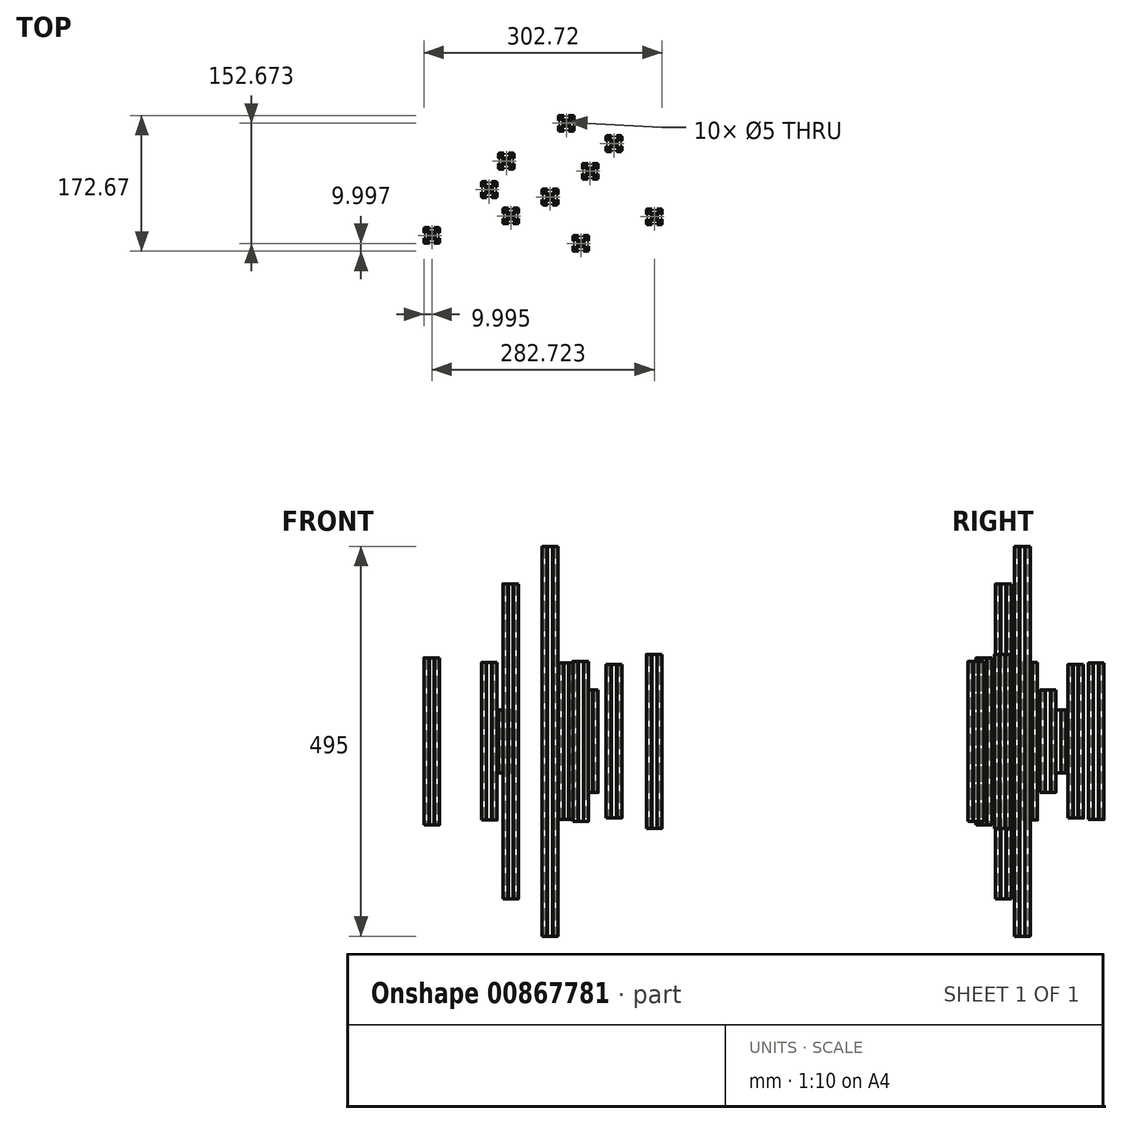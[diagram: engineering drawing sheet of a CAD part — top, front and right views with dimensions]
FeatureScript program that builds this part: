
annotation { "Feature Type Name" : "Feature", "Feature Type Description" : "" }
export const myFeature = defineFeature(function(context is Context, id is Id, definition is map)
    precondition{}
    {
        {
            var Q0;
            Q0=qCreatedBy(makeId("Top.planeOp"),FACE);
            var sketch = newSketch(context, id + "F0", { "sketchPlane" : qUnion([Q0])});
            skCircle(sketch, "E0", {"center": v(-10.22, 3.28) * mm, "radius": 2.5 * mm});
            skLineSegment(sketch, "E1.bottom", {"start": v(-1.72, -6.72) * mm, "end": v(-6.12, -6.72) * mm});
            skLineSegment(sketch, "E1.top", {"start": v(-1.72, 13.28) * mm, "end": v(-6.12, 13.28) * mm});
            skLineSegment(sketch, "E1.left", {"start": v(-0.22, -5.22) * mm, "end": v(-0.22, -0.32) * mm});
            skLineSegment(sketch, "E2.bottom", {"start": v(-8.21, -0.62) * mm, "end": v(-12.24, -0.62) * mm});
            skLineSegment(sketch, "E2.top", {"start": v(-8.21, 7.18) * mm, "end": v(-12.24, 7.18) * mm});
            skLineSegment(sketch, "E2.left", {"start": v(-6.32, 1.27) * mm, "end": v(-6.32, 5.3) * mm});
            skLineSegment(sketch, "E2.right", {"start": v(-14.12, 1.27) * mm, "end": v(-14.12, 5.3) * mm});
            skLineSegment(sketch, "E3.bottom", {"start": v(-1.72, 13.28) * mm, "end": v(-4.72, 13.28) * mm});
            skLineSegment(sketch, "E3.left", {"start": v(-0.22, 11.78) * mm, "end": v(-0.22, 8.78) * mm});
            skLineSegment(sketch, "E3.right", {"start": v(-4.72, 11.48) * mm, "end": v(-4.72, 9.84) * mm});
            skLineSegment(sketch, "E4", {"start": v(-5.74, 6.7) * mm, "end": v(-3.66, 8.78) * mm});
            skLineSegment(sketch, "E5.MirrorCS", {"start": v(-6.8, 7.77) * mm, "end": v(-4.72, 9.84) * mm});
            skLineSegment(sketch, "E6", {"start": v(-2.02, 8.78) * mm, "end": v(-2.02, 6.38) * mm});
            skLineSegment(sketch, "E7", {"start": v(-0.52, 6.88) * mm, "end": v(-0.22, 6.88) * mm});
            skLineSegment(sketch, "E8", {"start": v(-2.02, 6.38) * mm, "end": v(-0.72, 6.38) * mm});
            skLineSegment(sketch, "E9", {"start": v(-0.72, 6.68) * mm, "end": v(-0.72, 6.38) * mm});
            skPoint(sketch, "E10.visualSharp", {"position": v(-0.72, 6.88) * mm});
            skArc(sketch, "E10.filletArc", {"start": v(-0.52, 6.88) * mm, "mid": v(-0.67, 6.82) * mm, "end": v(-0.72, 6.68) * mm});
            skPoint(sketch, "E11.newPointA", {"position": v(-6.32, 6.12) * mm});
            skArc(sketch, "E11.filletArc", {"start": v(-5.74, 6.7) * mm, "mid": v(-6.17, 6.06) * mm, "end": v(-6.32, 5.3) * mm});
            skPoint(sketch, "E12.newPointA", {"position": v(-7.39, 7.18) * mm});
            skPoint(sketch, "E12.newPointB", {"position": v(-6.32, 7.18) * mm});
            skArc(sketch, "E12.filletArc", {"start": v(-8.21, 7.18) * mm, "mid": v(-7.45, 7.33) * mm, "end": v(-6.8, 7.77) * mm});
            skLineSegment(sketch, "E13.MirrorCS", {"start": v(-4.72, 11.48) * mm, "end": v(-7.12, 11.48) * mm});
            skLineSegment(sketch, "E14.MirrorCS", {"start": v(-7.12, 11.48) * mm, "end": v(-7.12, 12.78) * mm});
            skPoint(sketch, "E15.visualSharp", {"position": v(-0.22, 13.28) * mm});
            skArc(sketch, "E15.filletArc", {"start": v(-0.22, 11.78) * mm, "mid": v(-0.66, 12.84) * mm, "end": v(-1.72, 13.28) * mm});
            skLineSegment(sketch, "E16.trimOffspring", {"start": v(-2.02, 8.78) * mm, "end": v(-3.66, 8.78) * mm});
            skLineSegment(sketch, "E17.MirrorCS", {"start": v(-0.52, -0.32) * mm, "end": v(-0.22, -0.32) * mm});
            skArc(sketch, "E18.MirrorCS", {"start": v(-0.52, -0.32) * mm, "mid": v(-0.67, -0.26) * mm, "end": v(-0.72, -0.12) * mm});
            skLineSegment(sketch, "E19.MirrorCS", {"start": v(-0.72, -0.12) * mm, "end": v(-0.72, 0.18) * mm});
            skArc(sketch, "E20.MirrorCS", {"start": v(-5.74, -0.14) * mm, "mid": v(-6.17, 0.5) * mm, "end": v(-6.32, 1.27) * mm});
            skLineSegment(sketch, "E21.MirrorCS", {"start": v(-2.02, -2.22) * mm, "end": v(-3.66, -2.22) * mm});
            skLineSegment(sketch, "E22.MirrorCS", {"start": v(-2.02, 0.18) * mm, "end": v(-0.72, 0.18) * mm});
            skLineSegment(sketch, "E23.MirrorCS", {"start": v(-1.72, -6.72) * mm, "end": v(-4.72, -6.72) * mm});
            skPoint(sketch, "E24.MirrorP", {"position": v(-0.72, -0.32) * mm});
            skLineSegment(sketch, "E25.MirrorCS", {"start": v(-7.12, -4.92) * mm, "end": v(-7.12, -6.22) * mm});
            skLineSegment(sketch, "E26.MirrorCS", {"start": v(-4.72, -4.92) * mm, "end": v(-7.12, -4.92) * mm});
            skLineSegment(sketch, "E27.MirrorCS", {"start": v(-2.02, -2.22) * mm, "end": v(-2.02, 0.18) * mm});
            skLineSegment(sketch, "E28.MirrorCS", {"start": v(-0.22, -5.22) * mm, "end": v(-0.22, -2.22) * mm});
            skLineSegment(sketch, "E29.MirrorCS", {"start": v(-5.74, -0.14) * mm, "end": v(-3.66, -2.22) * mm});
            skPoint(sketch, "E30.MirrorP", {"position": v(-6.32, 0.44) * mm});
            skPoint(sketch, "E31.MirrorP", {"position": v(-0.22, -6.72) * mm});
            skPoint(sketch, "E32.MirrorP", {"position": v(-6.32, -0.62) * mm});
            skLineSegment(sketch, "E33.MirrorCS", {"start": v(-6.8, -1.2) * mm, "end": v(-4.72, -3.28) * mm});
            skPoint(sketch, "E34.MirrorP", {"position": v(-7.39, -0.62) * mm});
            skArc(sketch, "E35.MirrorCS", {"start": v(-0.22, -5.22) * mm, "mid": v(-0.66, -6.28) * mm, "end": v(-1.72, -6.72) * mm});
            skLineSegment(sketch, "E36.MirrorCS", {"start": v(-4.72, -4.92) * mm, "end": v(-4.72, -3.28) * mm});
            skArc(sketch, "E37.MirrorCS", {"start": v(-8.21, -0.62) * mm, "mid": v(-7.45, -0.77) * mm, "end": v(-6.8, -1.2) * mm});
            skLineSegment(sketch, "E38.trimOffspring", {"start": v(-0.22, 6.88) * mm, "end": v(-0.22, 11.78) * mm});
            skLineSegment(sketch, "E39.MirrorCS", {"start": v(-6.62, 12.98) * mm, "end": v(-6.62, 13.28) * mm});
            skArc(sketch, "E40.MirrorCS", {"start": v(-6.62, 12.98) * mm, "mid": v(-6.68, 12.84) * mm, "end": v(-6.82, 12.78) * mm});
            skLineSegment(sketch, "E41.MirrorCS", {"start": v(-6.82, 12.78) * mm, "end": v(-7.12, 12.78) * mm});
            skLineSegment(sketch, "E42", {"start": v(-6.12, 13.28) * mm, "end": v(-6.62, 13.28) * mm});
            skLineSegment(sketch, "E43.MirrorCS", {"start": v(-6.62, -6.42) * mm, "end": v(-6.62, -6.72) * mm});
            skLineSegment(sketch, "E44.MirrorCS", {"start": v(-6.82, -6.22) * mm, "end": v(-7.12, -6.22) * mm});
            skLineSegment(sketch, "E45.MirrorCS", {"start": v(-6.12, -6.72) * mm, "end": v(-6.62, -6.72) * mm});
            skArc(sketch, "E46.MirrorCS", {"start": v(-6.62, -6.42) * mm, "mid": v(-6.68, -6.28) * mm, "end": v(-6.82, -6.22) * mm});
            skArc(sketch, "E47.MirrorCS", {"start": v(-19.92, -0.32) * mm, "mid": v(-19.78, -0.26) * mm, "end": v(-19.72, -0.12) * mm});
            skLineSegment(sketch, "E48.MirrorCS", {"start": v(-19.92, 6.88) * mm, "end": v(-20.22, 6.88) * mm});
            skLineSegment(sketch, "E49.MirrorCS", {"start": v(-19.72, -0.12) * mm, "end": v(-19.72, 0.18) * mm});
            skArc(sketch, "E50.MirrorCS", {"start": v(-19.92, 6.88) * mm, "mid": v(-19.78, 6.82) * mm, "end": v(-19.72, 6.68) * mm});
            skLineSegment(sketch, "E51.MirrorCS", {"start": v(-19.72, 6.68) * mm, "end": v(-19.72, 6.38) * mm});
            skLineSegment(sketch, "E52.MirrorCS", {"start": v(-19.92, -0.32) * mm, "end": v(-20.22, -0.32) * mm});
            skLineSegment(sketch, "E53.MirrorCS", {"start": v(-14.32, 13.28) * mm, "end": v(-13.82, 13.28) * mm});
            skArc(sketch, "E54.MirrorCS", {"start": v(-20.22, -5.22) * mm, "mid": v(-19.79, -6.28) * mm, "end": v(-18.72, -6.72) * mm});
            skLineSegment(sketch, "E55.MirrorCS", {"start": v(-13.82, 12.98) * mm, "end": v(-13.82, 13.28) * mm});
            skArc(sketch, "E56.MirrorCS", {"start": v(-14.71, 6.7) * mm, "mid": v(-14.28, 6.06) * mm, "end": v(-14.12, 5.3) * mm});
            skLineSegment(sketch, "E57.MirrorCS", {"start": v(-13.62, -6.22) * mm, "end": v(-13.32, -6.22) * mm});
            skLineSegment(sketch, "E58.MirrorCS", {"start": v(-13.32, 11.48) * mm, "end": v(-13.32, 12.78) * mm});
            skLineSegment(sketch, "E59.MirrorCS", {"start": v(-12.24, 7.18) * mm, "end": v(-8.21, 7.18) * mm});
            skLineSegment(sketch, "E60.MirrorCS", {"start": v(-18.42, 0.18) * mm, "end": v(-19.72, 0.18) * mm});
            skLineSegment(sketch, "E61.MirrorCS", {"start": v(-18.42, 6.38) * mm, "end": v(-19.72, 6.38) * mm});
            skLineSegment(sketch, "E62.MirrorCS", {"start": v(-13.62, 12.78) * mm, "end": v(-13.32, 12.78) * mm});
            skArc(sketch, "E63.MirrorCS", {"start": v(-14.71, -0.14) * mm, "mid": v(-14.28, 0.5) * mm, "end": v(-14.12, 1.27) * mm});
            skArc(sketch, "E64.MirrorCS", {"start": v(-13.82, -6.42) * mm, "mid": v(-13.77, -6.28) * mm, "end": v(-13.62, -6.22) * mm});
            skArc(sketch, "E65.MirrorCS", {"start": v(-13.82, 12.98) * mm, "mid": v(-13.77, 12.84) * mm, "end": v(-13.62, 12.78) * mm});
            skLineSegment(sketch, "E66.MirrorCS", {"start": v(-13.82, -6.42) * mm, "end": v(-13.82, -6.72) * mm});
            skLineSegment(sketch, "E67.MirrorCS", {"start": v(-12.24, -0.62) * mm, "end": v(-8.21, -0.62) * mm});
            skLineSegment(sketch, "E68.MirrorCS", {"start": v(-14.32, -6.72) * mm, "end": v(-13.82, -6.72) * mm});
            skLineSegment(sketch, "E69.MirrorCS", {"start": v(-13.32, -4.92) * mm, "end": v(-13.32, -6.22) * mm});
            skArc(sketch, "E70.MirrorCS", {"start": v(-12.24, 7.18) * mm, "mid": v(-13, 7.33) * mm, "end": v(-13.65, 7.77) * mm});
            skPoint(sketch, "E71.MirrorP", {"position": v(-20.22, -6.72) * mm});
            skLineSegment(sketch, "E72.MirrorCS", {"start": v(-18.72, -6.72) * mm, "end": v(-14.32, -6.72) * mm});
            skPoint(sketch, "E73.MirrorP", {"position": v(-14.12, -0.62) * mm});
            skLineSegment(sketch, "E74.MirrorCS", {"start": v(-18.72, 13.28) * mm, "end": v(-14.32, 13.28) * mm});
            skArc(sketch, "E75.MirrorCS", {"start": v(-12.24, -0.62) * mm, "mid": v(-13, -0.77) * mm, "end": v(-13.65, -1.2) * mm});
            skArc(sketch, "E76.MirrorCS", {"start": v(-20.22, 11.78) * mm, "mid": v(-19.79, 12.84) * mm, "end": v(-18.72, 13.28) * mm});
            skPoint(sketch, "E77.MirrorP", {"position": v(-14.12, 0.44) * mm});
            skLineSegment(sketch, "E78.MirrorCS", {"start": v(-15.72, 11.48) * mm, "end": v(-15.72, 9.84) * mm});
            skLineSegment(sketch, "E79.MirrorCS", {"start": v(-13.65, 7.77) * mm, "end": v(-15.72, 9.84) * mm});
            skPoint(sketch, "E80.MirrorP", {"position": v(-14.12, 6.12) * mm});
            skLineSegment(sketch, "E81.MirrorCS", {"start": v(-18.42, -2.22) * mm, "end": v(-18.42, 0.18) * mm});
            skLineSegment(sketch, "E82.MirrorCS", {"start": v(-14.71, -0.14) * mm, "end": v(-16.79, -2.22) * mm});
            skLineSegment(sketch, "E83.MirrorCS", {"start": v(-15.72, -4.92) * mm, "end": v(-13.32, -4.92) * mm});
            skLineSegment(sketch, "E84.MirrorCS", {"start": v(-18.42, -2.22) * mm, "end": v(-16.79, -2.22) * mm});
            skLineSegment(sketch, "E85.MirrorCS", {"start": v(-20.22, -5.22) * mm, "end": v(-20.22, -2.22) * mm});
            skLineSegment(sketch, "E86.MirrorCS", {"start": v(-18.72, 13.28) * mm, "end": v(-15.72, 13.28) * mm});
            skLineSegment(sketch, "E87.MirrorCS", {"start": v(-20.22, 6.88) * mm, "end": v(-20.22, 11.78) * mm});
            skLineSegment(sketch, "E88.MirrorCS", {"start": v(-15.72, 11.48) * mm, "end": v(-13.32, 11.48) * mm});
            skLineSegment(sketch, "E89.MirrorCS", {"start": v(-13.65, -1.2) * mm, "end": v(-15.72, -3.28) * mm});
            skPoint(sketch, "E90.MirrorP", {"position": v(-13.06, -0.62) * mm});
            skLineSegment(sketch, "E91.MirrorCS", {"start": v(-18.42, 8.78) * mm, "end": v(-18.42, 6.38) * mm});
            skLineSegment(sketch, "E92.MirrorCS", {"start": v(-20.22, 11.78) * mm, "end": v(-20.22, 8.78) * mm});
            skPoint(sketch, "E93.MirrorP", {"position": v(-19.72, -0.32) * mm});
            skPoint(sketch, "E94.MirrorP", {"position": v(-20.22, 13.28) * mm});
            skPoint(sketch, "E95.MirrorP", {"position": v(-19.72, 6.88) * mm});
            skLineSegment(sketch, "E96.MirrorCS", {"start": v(-14.71, 6.7) * mm, "end": v(-16.79, 8.78) * mm});
            skLineSegment(sketch, "E97.MirrorCS", {"start": v(-18.42, 8.78) * mm, "end": v(-16.79, 8.78) * mm});
            skLineSegment(sketch, "E98.MirrorCS", {"start": v(-20.22, -5.22) * mm, "end": v(-20.22, -0.32) * mm});
            skLineSegment(sketch, "E99.MirrorCS", {"start": v(-18.72, -6.72) * mm, "end": v(-15.72, -6.72) * mm});
            skPoint(sketch, "E100.MirrorP", {"position": v(-14.12, 7.18) * mm});
            skPoint(sketch, "E101.MirrorP", {"position": v(-13.06, 7.18) * mm});
            skLineSegment(sketch, "E102.MirrorCS", {"start": v(-15.72, -4.92) * mm, "end": v(-15.72, -3.28) * mm});
            skSolve(sketch);
        }
        {
            var Q0;
            Q0=makeQuery(id+"F0.imprint","IMPRINT",FACE,{"disambiguationData":[TD([[makeQuery(id+"F0.imprint","IMPRINT",EDGE,{"derivedFrom":sQuery(id+"F0.wireOp",EDGE,"E1.bottom")}),-1.0]])]});
            extrude(context, id + "F1", {"entities" : qUnion([Q0]), "endBound" : BoundingType.SYMMETRIC, "depth" : 495 * mm, "offsetDistance" : 25 * mm});
        }
        {
            var Q0;
            Q0=qCreatedBy(makeId("Top.planeOp"),FACE);
            var sketch = newSketch(context, id + "F2", { "sketchPlane" : qUnion([Q0])});
            skCircle(sketch, "E103", {"center": v(-87.46, 12.57) * mm, "radius": 2.5 * mm});
            skLineSegment(sketch, "E104.bottom", {"start": v(-78.96, 2.57) * mm, "end": v(-83.36, 2.57) * mm});
            skLineSegment(sketch, "E104.top", {"start": v(-78.96, 22.57) * mm, "end": v(-83.36, 22.57) * mm});
            skLineSegment(sketch, "E104.left", {"start": v(-77.46, 4.07) * mm, "end": v(-77.46, 8.97) * mm});
            skLineSegment(sketch, "E105.bottom", {"start": v(-85.45, 8.67) * mm, "end": v(-89.47, 8.67) * mm});
            skLineSegment(sketch, "E105.top", {"start": v(-85.45, 16.47) * mm, "end": v(-89.47, 16.47) * mm});
            skLineSegment(sketch, "E105.left", {"start": v(-83.56, 10.56) * mm, "end": v(-83.56, 14.58) * mm});
            skLineSegment(sketch, "E105.right", {"start": v(-91.36, 10.56) * mm, "end": v(-91.36, 14.58) * mm});
            skLineSegment(sketch, "E106.bottom", {"start": v(-78.96, 22.57) * mm, "end": v(-81.96, 22.57) * mm});
            skLineSegment(sketch, "E106.left", {"start": v(-77.46, 21.07) * mm, "end": v(-77.46, 18.07) * mm});
            skLineSegment(sketch, "E106.right", {"start": v(-81.96, 20.77) * mm, "end": v(-81.96, 19.13) * mm});
            skLineSegment(sketch, "E107", {"start": v(-82.97, 16) * mm, "end": v(-80.9, 18.07) * mm});
            skLineSegment(sketch, "E108.MirrorCS", {"start": v(-84.04, 17.06) * mm, "end": v(-81.96, 19.13) * mm});
            skLineSegment(sketch, "E109", {"start": v(-79.26, 18.07) * mm, "end": v(-79.26, 15.67) * mm});
            skLineSegment(sketch, "E110", {"start": v(-77.76, 16.17) * mm, "end": v(-77.46, 16.17) * mm});
            skLineSegment(sketch, "E111", {"start": v(-79.26, 15.67) * mm, "end": v(-77.96, 15.67) * mm});
            skLineSegment(sketch, "E112", {"start": v(-77.96, 15.97) * mm, "end": v(-77.96, 15.67) * mm});
            skPoint(sketch, "E113.visualSharp", {"position": v(-77.96, 16.17) * mm});
            skArc(sketch, "E113.filletArc", {"start": v(-77.76, 16.17) * mm, "mid": v(-77.9, 16.11) * mm, "end": v(-77.96, 15.97) * mm});
            skPoint(sketch, "E114.newPointA", {"position": v(-83.56, 15.4) * mm});
            skArc(sketch, "E114.filletArc", {"start": v(-82.97, 16) * mm, "mid": v(-83.4, 15.35) * mm, "end": v(-83.56, 14.58) * mm});
            skPoint(sketch, "E115.newPointA", {"position": v(-84.62, 16.47) * mm});
            skPoint(sketch, "E115.newPointB", {"position": v(-83.56, 16.47) * mm});
            skArc(sketch, "E115.filletArc", {"start": v(-85.45, 16.47) * mm, "mid": v(-84.68, 16.62) * mm, "end": v(-84.04, 17.06) * mm});
            skLineSegment(sketch, "E116.MirrorCS", {"start": v(-81.96, 20.77) * mm, "end": v(-84.36, 20.77) * mm});
            skLineSegment(sketch, "E117.MirrorCS", {"start": v(-84.36, 20.77) * mm, "end": v(-84.36, 22.07) * mm});
            skPoint(sketch, "E118.visualSharp", {"position": v(-77.46, 22.57) * mm});
            skArc(sketch, "E118.filletArc", {"start": v(-77.46, 21.07) * mm, "mid": v(-77.9, 22.13) * mm, "end": v(-78.96, 22.57) * mm});
            skLineSegment(sketch, "E119.trimOffspring", {"start": v(-79.26, 18.07) * mm, "end": v(-80.9, 18.07) * mm});
            skLineSegment(sketch, "E120.MirrorCS", {"start": v(-77.76, 8.97) * mm, "end": v(-77.46, 8.97) * mm});
            skArc(sketch, "E121.MirrorCS", {"start": v(-77.76, 8.97) * mm, "mid": v(-77.9, 9.03) * mm, "end": v(-77.96, 9.17) * mm});
            skLineSegment(sketch, "E122.MirrorCS", {"start": v(-77.96, 9.17) * mm, "end": v(-77.96, 9.47) * mm});
            skArc(sketch, "E123.MirrorCS", {"start": v(-82.97, 9.15) * mm, "mid": v(-83.4, 9.8) * mm, "end": v(-83.56, 10.56) * mm});
            skLineSegment(sketch, "E124.MirrorCS", {"start": v(-79.26, 7.07) * mm, "end": v(-80.9, 7.07) * mm});
            skLineSegment(sketch, "E125.MirrorCS", {"start": v(-79.26, 9.47) * mm, "end": v(-77.96, 9.47) * mm});
            skLineSegment(sketch, "E126.MirrorCS", {"start": v(-78.96, 2.57) * mm, "end": v(-81.96, 2.57) * mm});
            skPoint(sketch, "E127.MirrorP", {"position": v(-77.96, 8.97) * mm});
            skLineSegment(sketch, "E128.MirrorCS", {"start": v(-84.36, 4.37) * mm, "end": v(-84.36, 3.07) * mm});
            skLineSegment(sketch, "E129.MirrorCS", {"start": v(-81.96, 4.37) * mm, "end": v(-84.36, 4.37) * mm});
            skLineSegment(sketch, "E130.MirrorCS", {"start": v(-79.26, 7.07) * mm, "end": v(-79.26, 9.47) * mm});
            skLineSegment(sketch, "E131.MirrorCS", {"start": v(-77.46, 4.07) * mm, "end": v(-77.46, 7.07) * mm});
            skLineSegment(sketch, "E132.MirrorCS", {"start": v(-82.97, 9.15) * mm, "end": v(-80.9, 7.07) * mm});
            skPoint(sketch, "E133.MirrorP", {"position": v(-83.56, 9.73) * mm});
            skPoint(sketch, "E134.MirrorP", {"position": v(-77.46, 2.57) * mm});
            skPoint(sketch, "E135.MirrorP", {"position": v(-83.56, 8.67) * mm});
            skLineSegment(sketch, "E136.MirrorCS", {"start": v(-84.04, 8.08) * mm, "end": v(-81.96, 6) * mm});
            skPoint(sketch, "E137.MirrorP", {"position": v(-84.62, 8.67) * mm});
            skArc(sketch, "E138.MirrorCS", {"start": v(-77.46, 4.07) * mm, "mid": v(-77.9, 3) * mm, "end": v(-78.96, 2.57) * mm});
            skLineSegment(sketch, "E139.MirrorCS", {"start": v(-81.96, 4.37) * mm, "end": v(-81.96, 6) * mm});
            skArc(sketch, "E140.MirrorCS", {"start": v(-85.45, 8.67) * mm, "mid": v(-84.68, 8.52) * mm, "end": v(-84.04, 8.08) * mm});
            skLineSegment(sketch, "E141.trimOffspring", {"start": v(-77.46, 16.17) * mm, "end": v(-77.46, 21.07) * mm});
            skLineSegment(sketch, "E142.MirrorCS", {"start": v(-83.86, 22.27) * mm, "end": v(-83.86, 22.57) * mm});
            skArc(sketch, "E143.MirrorCS", {"start": v(-83.86, 22.27) * mm, "mid": v(-83.92, 22.13) * mm, "end": v(-84.06, 22.07) * mm});
            skLineSegment(sketch, "E144.MirrorCS", {"start": v(-84.06, 22.07) * mm, "end": v(-84.36, 22.07) * mm});
            skLineSegment(sketch, "E145", {"start": v(-83.36, 22.57) * mm, "end": v(-83.86, 22.57) * mm});
            skLineSegment(sketch, "E146.MirrorCS", {"start": v(-83.86, 2.87) * mm, "end": v(-83.86, 2.57) * mm});
            skLineSegment(sketch, "E147.MirrorCS", {"start": v(-84.06, 3.07) * mm, "end": v(-84.36, 3.07) * mm});
            skLineSegment(sketch, "E148.MirrorCS", {"start": v(-83.36, 2.57) * mm, "end": v(-83.86, 2.57) * mm});
            skArc(sketch, "E149.MirrorCS", {"start": v(-83.86, 2.87) * mm, "mid": v(-83.92, 3.01) * mm, "end": v(-84.06, 3.07) * mm});
            skArc(sketch, "E150.MirrorCS", {"start": v(-97.16, 8.97) * mm, "mid": v(-97.02, 9.03) * mm, "end": v(-96.96, 9.17) * mm});
            skLineSegment(sketch, "E151.MirrorCS", {"start": v(-97.16, 16.17) * mm, "end": v(-97.46, 16.17) * mm});
            skLineSegment(sketch, "E152.MirrorCS", {"start": v(-96.96, 9.17) * mm, "end": v(-96.96, 9.47) * mm});
            skArc(sketch, "E153.MirrorCS", {"start": v(-97.16, 16.17) * mm, "mid": v(-97.02, 16.11) * mm, "end": v(-96.96, 15.97) * mm});
            skLineSegment(sketch, "E154.MirrorCS", {"start": v(-96.96, 15.97) * mm, "end": v(-96.96, 15.67) * mm});
            skLineSegment(sketch, "E155.MirrorCS", {"start": v(-97.16, 8.97) * mm, "end": v(-97.46, 8.97) * mm});
            skLineSegment(sketch, "E156.MirrorCS", {"start": v(-91.56, 22.57) * mm, "end": v(-91.06, 22.57) * mm});
            skArc(sketch, "E157.MirrorCS", {"start": v(-97.46, 4.07) * mm, "mid": v(-97.02, 3) * mm, "end": v(-95.96, 2.57) * mm});
            skLineSegment(sketch, "E158.MirrorCS", {"start": v(-91.06, 22.27) * mm, "end": v(-91.06, 22.57) * mm});
            skArc(sketch, "E159.MirrorCS", {"start": v(-91.95, 16) * mm, "mid": v(-91.51, 15.35) * mm, "end": v(-91.36, 14.58) * mm});
            skLineSegment(sketch, "E160.MirrorCS", {"start": v(-90.86, 3.07) * mm, "end": v(-90.56, 3.07) * mm});
            skLineSegment(sketch, "E161.MirrorCS", {"start": v(-90.56, 20.77) * mm, "end": v(-90.56, 22.07) * mm});
            skLineSegment(sketch, "E162.MirrorCS", {"start": v(-89.47, 16.47) * mm, "end": v(-85.45, 16.47) * mm});
            skLineSegment(sketch, "E163.MirrorCS", {"start": v(-95.66, 9.47) * mm, "end": v(-96.96, 9.47) * mm});
            skLineSegment(sketch, "E164.MirrorCS", {"start": v(-95.66, 15.67) * mm, "end": v(-96.96, 15.67) * mm});
            skLineSegment(sketch, "E165.MirrorCS", {"start": v(-90.86, 22.07) * mm, "end": v(-90.56, 22.07) * mm});
            skArc(sketch, "E166.MirrorCS", {"start": v(-91.95, 9.15) * mm, "mid": v(-91.51, 9.8) * mm, "end": v(-91.36, 10.56) * mm});
            skArc(sketch, "E167.MirrorCS", {"start": v(-91.06, 2.87) * mm, "mid": v(-91, 3.01) * mm, "end": v(-90.86, 3.07) * mm});
            skArc(sketch, "E168.MirrorCS", {"start": v(-91.06, 22.27) * mm, "mid": v(-91, 22.13) * mm, "end": v(-90.86, 22.07) * mm});
            skLineSegment(sketch, "E169.MirrorCS", {"start": v(-91.06, 2.87) * mm, "end": v(-91.06, 2.57) * mm});
            skLineSegment(sketch, "E170.MirrorCS", {"start": v(-89.47, 8.67) * mm, "end": v(-85.45, 8.67) * mm});
            skLineSegment(sketch, "E171.MirrorCS", {"start": v(-91.56, 2.57) * mm, "end": v(-91.06, 2.57) * mm});
            skLineSegment(sketch, "E172.MirrorCS", {"start": v(-90.56, 4.37) * mm, "end": v(-90.56, 3.07) * mm});
            skArc(sketch, "E173.MirrorCS", {"start": v(-89.47, 16.47) * mm, "mid": v(-90.24, 16.62) * mm, "end": v(-90.89, 17.06) * mm});
            skPoint(sketch, "E174.MirrorP", {"position": v(-97.46, 2.57) * mm});
            skLineSegment(sketch, "E175.MirrorCS", {"start": v(-95.96, 2.57) * mm, "end": v(-91.56, 2.57) * mm});
            skPoint(sketch, "E176.MirrorP", {"position": v(-91.36, 8.67) * mm});
            skLineSegment(sketch, "E177.MirrorCS", {"start": v(-95.96, 22.57) * mm, "end": v(-91.56, 22.57) * mm});
            skArc(sketch, "E178.MirrorCS", {"start": v(-89.47, 8.67) * mm, "mid": v(-90.24, 8.52) * mm, "end": v(-90.89, 8.08) * mm});
            skArc(sketch, "E179.MirrorCS", {"start": v(-97.46, 21.07) * mm, "mid": v(-97.02, 22.13) * mm, "end": v(-95.96, 22.57) * mm});
            skPoint(sketch, "E180.MirrorP", {"position": v(-91.36, 9.73) * mm});
            skLineSegment(sketch, "E181.MirrorCS", {"start": v(-92.96, 20.77) * mm, "end": v(-92.96, 19.13) * mm});
            skLineSegment(sketch, "E182.MirrorCS", {"start": v(-90.89, 17.06) * mm, "end": v(-92.96, 19.13) * mm});
            skPoint(sketch, "E183.MirrorP", {"position": v(-91.36, 15.4) * mm});
            skLineSegment(sketch, "E184.MirrorCS", {"start": v(-95.66, 7.07) * mm, "end": v(-95.66, 9.47) * mm});
            skLineSegment(sketch, "E185.MirrorCS", {"start": v(-91.95, 9.15) * mm, "end": v(-94.02, 7.07) * mm});
            skLineSegment(sketch, "E186.MirrorCS", {"start": v(-92.96, 4.37) * mm, "end": v(-90.56, 4.37) * mm});
            skLineSegment(sketch, "E187.MirrorCS", {"start": v(-95.66, 7.07) * mm, "end": v(-94.02, 7.07) * mm});
            skLineSegment(sketch, "E188.MirrorCS", {"start": v(-97.46, 4.07) * mm, "end": v(-97.46, 7.07) * mm});
            skLineSegment(sketch, "E189.MirrorCS", {"start": v(-95.96, 22.57) * mm, "end": v(-92.96, 22.57) * mm});
            skLineSegment(sketch, "E190.MirrorCS", {"start": v(-97.46, 16.17) * mm, "end": v(-97.46, 21.07) * mm});
            skLineSegment(sketch, "E191.MirrorCS", {"start": v(-92.96, 20.77) * mm, "end": v(-90.56, 20.77) * mm});
            skLineSegment(sketch, "E192.MirrorCS", {"start": v(-90.89, 8.08) * mm, "end": v(-92.96, 6) * mm});
            skPoint(sketch, "E193.MirrorP", {"position": v(-90.3, 8.67) * mm});
            skLineSegment(sketch, "E194.MirrorCS", {"start": v(-95.66, 18.07) * mm, "end": v(-95.66, 15.67) * mm});
            skLineSegment(sketch, "E195.MirrorCS", {"start": v(-97.46, 21.07) * mm, "end": v(-97.46, 18.07) * mm});
            skPoint(sketch, "E196.MirrorP", {"position": v(-96.96, 8.97) * mm});
            skPoint(sketch, "E197.MirrorP", {"position": v(-97.46, 22.57) * mm});
            skPoint(sketch, "E198.MirrorP", {"position": v(-96.96, 16.17) * mm});
            skLineSegment(sketch, "E199.MirrorCS", {"start": v(-91.95, 16) * mm, "end": v(-94.02, 18.07) * mm});
            skLineSegment(sketch, "E200.MirrorCS", {"start": v(-95.66, 18.07) * mm, "end": v(-94.02, 18.07) * mm});
            skLineSegment(sketch, "E201.MirrorCS", {"start": v(-97.46, 4.07) * mm, "end": v(-97.46, 8.97) * mm});
            skLineSegment(sketch, "E202.MirrorCS", {"start": v(-95.96, 2.57) * mm, "end": v(-92.96, 2.57) * mm});
            skPoint(sketch, "E203.MirrorP", {"position": v(-91.36, 16.47) * mm});
            skPoint(sketch, "E204.MirrorP", {"position": v(-90.3, 16.47) * mm});
            skLineSegment(sketch, "E205.MirrorCS", {"start": v(-92.96, 4.37) * mm, "end": v(-92.96, 6) * mm});
            skSolve(sketch);
        }
        {
            var Q0;
            Q0=makeQuery(id+"F2.imprint","IMPRINT",FACE,{"disambiguationData":[TD([[makeQuery(id+"F2.imprint","IMPRINT",EDGE,{"derivedFrom":sQuery(id+"F2.wireOp",EDGE,"E104.bottom")}),-1.0]])]});
            extrude(context, id + "F3", {"entities" : qUnion([Q0]), "endBound" : BoundingType.SYMMETRIC, "depth" : 200 * mm, "offsetDistance" : 25 * mm});
        }
        {
            var Q0;
            Q0=qCreatedBy(makeId("Top.planeOp"),FACE);
            var sketch = newSketch(context, id + "F4", { "sketchPlane" : qUnion([Q0])});
            skCircle(sketch, "E206", {"center": v(40.83, 35.88) * mm, "radius": 2.5 * mm});
            skLineSegment(sketch, "E207.bottom", {"start": v(49.33, 25.88) * mm, "end": v(44.93, 25.88) * mm});
            skLineSegment(sketch, "E207.top", {"start": v(49.33, 45.88) * mm, "end": v(44.93, 45.88) * mm});
            skLineSegment(sketch, "E207.left", {"start": v(50.83, 27.38) * mm, "end": v(50.83, 32.28) * mm});
            skLineSegment(sketch, "E208.bottom", {"start": v(42.84, 31.98) * mm, "end": v(38.82, 31.98) * mm});
            skLineSegment(sketch, "E208.top", {"start": v(42.84, 39.78) * mm, "end": v(38.82, 39.78) * mm});
            skLineSegment(sketch, "E208.left", {"start": v(44.73, 33.87) * mm, "end": v(44.73, 37.9) * mm});
            skLineSegment(sketch, "E208.right", {"start": v(36.93, 33.87) * mm, "end": v(36.93, 37.9) * mm});
            skLineSegment(sketch, "E209.bottom", {"start": v(49.33, 45.88) * mm, "end": v(46.33, 45.88) * mm});
            skLineSegment(sketch, "E209.left", {"start": v(50.83, 44.38) * mm, "end": v(50.83, 41.38) * mm});
            skLineSegment(sketch, "E209.right", {"start": v(46.33, 44.08) * mm, "end": v(46.33, 42.45) * mm});
            skLineSegment(sketch, "E210", {"start": v(45.31, 39.31) * mm, "end": v(47.39, 41.38) * mm});
            skLineSegment(sketch, "E211.MirrorCS", {"start": v(44.25, 40.37) * mm, "end": v(46.33, 42.45) * mm});
            skLineSegment(sketch, "E212", {"start": v(49.03, 41.38) * mm, "end": v(49.03, 38.98) * mm});
            skLineSegment(sketch, "E213", {"start": v(50.53, 39.48) * mm, "end": v(50.83, 39.48) * mm});
            skLineSegment(sketch, "E214", {"start": v(49.03, 38.98) * mm, "end": v(50.33, 38.98) * mm});
            skLineSegment(sketch, "E215", {"start": v(50.33, 39.28) * mm, "end": v(50.33, 38.98) * mm});
            skPoint(sketch, "E216.visualSharp", {"position": v(50.33, 39.48) * mm});
            skArc(sketch, "E216.filletArc", {"start": v(50.53, 39.48) * mm, "mid": v(50.39, 39.43) * mm, "end": v(50.33, 39.28) * mm});
            skPoint(sketch, "E217.newPointA", {"position": v(44.73, 38.72) * mm});
            skArc(sketch, "E217.filletArc", {"start": v(45.31, 39.31) * mm, "mid": v(44.88, 38.66) * mm, "end": v(44.73, 37.9) * mm});
            skPoint(sketch, "E218.newPointA", {"position": v(43.67, 39.78) * mm});
            skPoint(sketch, "E218.newPointB", {"position": v(44.73, 39.78) * mm});
            skArc(sketch, "E218.filletArc", {"start": v(42.84, 39.78) * mm, "mid": v(43.6, 39.94) * mm, "end": v(44.25, 40.37) * mm});
            skLineSegment(sketch, "E219.MirrorCS", {"start": v(46.33, 44.08) * mm, "end": v(43.93, 44.08) * mm});
            skLineSegment(sketch, "E220.MirrorCS", {"start": v(43.93, 44.08) * mm, "end": v(43.93, 45.38) * mm});
            skPoint(sketch, "E221.visualSharp", {"position": v(50.83, 45.88) * mm});
            skArc(sketch, "E221.filletArc", {"start": v(50.83, 44.38) * mm, "mid": v(50.39, 45.45) * mm, "end": v(49.33, 45.88) * mm});
            skLineSegment(sketch, "E222.trimOffspring", {"start": v(49.03, 41.38) * mm, "end": v(47.39, 41.38) * mm});
            skLineSegment(sketch, "E223.MirrorCS", {"start": v(50.53, 32.28) * mm, "end": v(50.83, 32.28) * mm});
            skArc(sketch, "E224.MirrorCS", {"start": v(50.53, 32.28) * mm, "mid": v(50.39, 32.34) * mm, "end": v(50.33, 32.48) * mm});
            skLineSegment(sketch, "E225.MirrorCS", {"start": v(50.33, 32.48) * mm, "end": v(50.33, 32.78) * mm});
            skArc(sketch, "E226.MirrorCS", {"start": v(45.31, 32.46) * mm, "mid": v(44.88, 33.1) * mm, "end": v(44.73, 33.87) * mm});
            skLineSegment(sketch, "E227.MirrorCS", {"start": v(49.03, 30.38) * mm, "end": v(47.39, 30.38) * mm});
            skLineSegment(sketch, "E228.MirrorCS", {"start": v(49.03, 32.78) * mm, "end": v(50.33, 32.78) * mm});
            skLineSegment(sketch, "E229.MirrorCS", {"start": v(49.33, 25.88) * mm, "end": v(46.33, 25.88) * mm});
            skPoint(sketch, "E230.MirrorP", {"position": v(50.33, 32.28) * mm});
            skLineSegment(sketch, "E231.MirrorCS", {"start": v(43.93, 27.68) * mm, "end": v(43.93, 26.38) * mm});
            skLineSegment(sketch, "E232.MirrorCS", {"start": v(46.33, 27.68) * mm, "end": v(43.93, 27.68) * mm});
            skLineSegment(sketch, "E233.MirrorCS", {"start": v(49.03, 30.38) * mm, "end": v(49.03, 32.78) * mm});
            skLineSegment(sketch, "E234.MirrorCS", {"start": v(50.83, 27.38) * mm, "end": v(50.83, 30.38) * mm});
            skLineSegment(sketch, "E235.MirrorCS", {"start": v(45.31, 32.46) * mm, "end": v(47.39, 30.38) * mm});
            skPoint(sketch, "E236.MirrorP", {"position": v(44.73, 33.05) * mm});
            skPoint(sketch, "E237.MirrorP", {"position": v(50.83, 25.88) * mm});
            skPoint(sketch, "E238.MirrorP", {"position": v(44.73, 31.98) * mm});
            skLineSegment(sketch, "E239.MirrorCS", {"start": v(44.25, 31.4) * mm, "end": v(46.33, 29.32) * mm});
            skPoint(sketch, "E240.MirrorP", {"position": v(43.67, 31.98) * mm});
            skArc(sketch, "E241.MirrorCS", {"start": v(50.83, 27.38) * mm, "mid": v(50.39, 26.32) * mm, "end": v(49.33, 25.88) * mm});
            skLineSegment(sketch, "E242.MirrorCS", {"start": v(46.33, 27.68) * mm, "end": v(46.33, 29.32) * mm});
            skArc(sketch, "E243.MirrorCS", {"start": v(42.84, 31.98) * mm, "mid": v(43.6, 31.83) * mm, "end": v(44.25, 31.4) * mm});
            skLineSegment(sketch, "E244.trimOffspring", {"start": v(50.83, 39.48) * mm, "end": v(50.83, 44.38) * mm});
            skLineSegment(sketch, "E245.MirrorCS", {"start": v(44.43, 45.58) * mm, "end": v(44.43, 45.88) * mm});
            skArc(sketch, "E246.MirrorCS", {"start": v(44.43, 45.58) * mm, "mid": v(44.37, 45.44) * mm, "end": v(44.23, 45.38) * mm});
            skLineSegment(sketch, "E247.MirrorCS", {"start": v(44.23, 45.38) * mm, "end": v(43.93, 45.38) * mm});
            skLineSegment(sketch, "E248", {"start": v(44.93, 45.88) * mm, "end": v(44.43, 45.88) * mm});
            skLineSegment(sketch, "E249.MirrorCS", {"start": v(44.43, 26.18) * mm, "end": v(44.43, 25.88) * mm});
            skLineSegment(sketch, "E250.MirrorCS", {"start": v(44.23, 26.38) * mm, "end": v(43.93, 26.38) * mm});
            skLineSegment(sketch, "E251.MirrorCS", {"start": v(44.93, 25.88) * mm, "end": v(44.43, 25.88) * mm});
            skArc(sketch, "E252.MirrorCS", {"start": v(44.43, 26.18) * mm, "mid": v(44.37, 26.33) * mm, "end": v(44.23, 26.38) * mm});
            skArc(sketch, "E253.MirrorCS", {"start": v(31.13, 32.28) * mm, "mid": v(31.27, 32.34) * mm, "end": v(31.33, 32.48) * mm});
            skLineSegment(sketch, "E254.MirrorCS", {"start": v(31.13, 39.48) * mm, "end": v(30.83, 39.48) * mm});
            skLineSegment(sketch, "E255.MirrorCS", {"start": v(31.33, 32.48) * mm, "end": v(31.33, 32.78) * mm});
            skArc(sketch, "E256.MirrorCS", {"start": v(31.13, 39.48) * mm, "mid": v(31.27, 39.43) * mm, "end": v(31.33, 39.28) * mm});
            skLineSegment(sketch, "E257.MirrorCS", {"start": v(31.33, 39.28) * mm, "end": v(31.33, 38.98) * mm});
            skLineSegment(sketch, "E258.MirrorCS", {"start": v(31.13, 32.28) * mm, "end": v(30.83, 32.28) * mm});
            skLineSegment(sketch, "E259.MirrorCS", {"start": v(36.73, 45.88) * mm, "end": v(37.23, 45.88) * mm});
            skArc(sketch, "E260.MirrorCS", {"start": v(30.83, 27.38) * mm, "mid": v(31.27, 26.32) * mm, "end": v(32.33, 25.88) * mm});
            skLineSegment(sketch, "E261.MirrorCS", {"start": v(37.23, 45.58) * mm, "end": v(37.23, 45.88) * mm});
            skArc(sketch, "E262.MirrorCS", {"start": v(36.34, 39.31) * mm, "mid": v(36.78, 38.66) * mm, "end": v(36.93, 37.9) * mm});
            skLineSegment(sketch, "E263.MirrorCS", {"start": v(37.43, 26.38) * mm, "end": v(37.73, 26.38) * mm});
            skLineSegment(sketch, "E264.MirrorCS", {"start": v(37.73, 44.08) * mm, "end": v(37.73, 45.38) * mm});
            skLineSegment(sketch, "E265.MirrorCS", {"start": v(38.82, 39.78) * mm, "end": v(42.84, 39.78) * mm});
            skLineSegment(sketch, "E266.MirrorCS", {"start": v(32.63, 32.78) * mm, "end": v(31.33, 32.78) * mm});
            skLineSegment(sketch, "E267.MirrorCS", {"start": v(32.63, 38.98) * mm, "end": v(31.33, 38.98) * mm});
            skLineSegment(sketch, "E268.MirrorCS", {"start": v(37.43, 45.38) * mm, "end": v(37.73, 45.38) * mm});
            skArc(sketch, "E269.MirrorCS", {"start": v(36.34, 32.46) * mm, "mid": v(36.78, 33.1) * mm, "end": v(36.93, 33.87) * mm});
            skArc(sketch, "E270.MirrorCS", {"start": v(37.23, 26.18) * mm, "mid": v(37.29, 26.33) * mm, "end": v(37.43, 26.38) * mm});
            skArc(sketch, "E271.MirrorCS", {"start": v(37.23, 45.58) * mm, "mid": v(37.29, 45.44) * mm, "end": v(37.43, 45.38) * mm});
            skLineSegment(sketch, "E272.MirrorCS", {"start": v(37.23, 26.18) * mm, "end": v(37.23, 25.88) * mm});
            skLineSegment(sketch, "E273.MirrorCS", {"start": v(38.82, 31.98) * mm, "end": v(42.84, 31.98) * mm});
            skLineSegment(sketch, "E274.MirrorCS", {"start": v(36.73, 25.88) * mm, "end": v(37.23, 25.88) * mm});
            skLineSegment(sketch, "E275.MirrorCS", {"start": v(37.73, 27.68) * mm, "end": v(37.73, 26.38) * mm});
            skArc(sketch, "E276.MirrorCS", {"start": v(38.82, 39.78) * mm, "mid": v(38.05, 39.94) * mm, "end": v(37.4, 40.37) * mm});
            skPoint(sketch, "E277.MirrorP", {"position": v(30.83, 25.88) * mm});
            skLineSegment(sketch, "E278.MirrorCS", {"start": v(32.33, 25.88) * mm, "end": v(36.73, 25.88) * mm});
            skPoint(sketch, "E279.MirrorP", {"position": v(36.93, 31.98) * mm});
            skLineSegment(sketch, "E280.MirrorCS", {"start": v(32.33, 45.88) * mm, "end": v(36.73, 45.88) * mm});
            skArc(sketch, "E281.MirrorCS", {"start": v(38.82, 31.98) * mm, "mid": v(38.05, 31.83) * mm, "end": v(37.4, 31.4) * mm});
            skArc(sketch, "E282.MirrorCS", {"start": v(30.83, 44.38) * mm, "mid": v(31.27, 45.45) * mm, "end": v(32.33, 45.88) * mm});
            skPoint(sketch, "E283.MirrorP", {"position": v(36.93, 33.05) * mm});
            skLineSegment(sketch, "E284.MirrorCS", {"start": v(35.33, 44.08) * mm, "end": v(35.33, 42.45) * mm});
            skLineSegment(sketch, "E285.MirrorCS", {"start": v(37.4, 40.37) * mm, "end": v(35.33, 42.45) * mm});
            skPoint(sketch, "E286.MirrorP", {"position": v(36.93, 38.72) * mm});
            skLineSegment(sketch, "E287.MirrorCS", {"start": v(32.63, 30.38) * mm, "end": v(32.63, 32.78) * mm});
            skLineSegment(sketch, "E288.MirrorCS", {"start": v(36.34, 32.46) * mm, "end": v(34.27, 30.38) * mm});
            skLineSegment(sketch, "E289.MirrorCS", {"start": v(35.33, 27.68) * mm, "end": v(37.73, 27.68) * mm});
            skLineSegment(sketch, "E290.MirrorCS", {"start": v(32.63, 30.38) * mm, "end": v(34.27, 30.38) * mm});
            skLineSegment(sketch, "E291.MirrorCS", {"start": v(30.83, 27.38) * mm, "end": v(30.83, 30.38) * mm});
            skLineSegment(sketch, "E292.MirrorCS", {"start": v(32.33, 45.88) * mm, "end": v(35.33, 45.88) * mm});
            skLineSegment(sketch, "E293.MirrorCS", {"start": v(30.83, 39.48) * mm, "end": v(30.83, 44.38) * mm});
            skLineSegment(sketch, "E294.MirrorCS", {"start": v(35.33, 44.08) * mm, "end": v(37.73, 44.08) * mm});
            skLineSegment(sketch, "E295.MirrorCS", {"start": v(37.4, 31.4) * mm, "end": v(35.33, 29.32) * mm});
            skPoint(sketch, "E296.MirrorP", {"position": v(37.99, 31.98) * mm});
            skLineSegment(sketch, "E297.MirrorCS", {"start": v(32.63, 41.38) * mm, "end": v(32.63, 38.98) * mm});
            skLineSegment(sketch, "E298.MirrorCS", {"start": v(30.83, 44.38) * mm, "end": v(30.83, 41.38) * mm});
            skPoint(sketch, "E299.MirrorP", {"position": v(31.33, 32.28) * mm});
            skPoint(sketch, "E300.MirrorP", {"position": v(30.83, 45.88) * mm});
            skPoint(sketch, "E301.MirrorP", {"position": v(31.33, 39.48) * mm});
            skLineSegment(sketch, "E302.MirrorCS", {"start": v(36.34, 39.31) * mm, "end": v(34.27, 41.38) * mm});
            skLineSegment(sketch, "E303.MirrorCS", {"start": v(32.63, 41.38) * mm, "end": v(34.27, 41.38) * mm});
            skLineSegment(sketch, "E304.MirrorCS", {"start": v(30.83, 27.38) * mm, "end": v(30.83, 32.28) * mm});
            skLineSegment(sketch, "E305.MirrorCS", {"start": v(32.33, 25.88) * mm, "end": v(35.33, 25.88) * mm});
            skPoint(sketch, "E306.MirrorP", {"position": v(36.93, 39.78) * mm});
            skPoint(sketch, "E307.MirrorP", {"position": v(37.99, 39.78) * mm});
            skLineSegment(sketch, "E308.MirrorCS", {"start": v(35.33, 27.68) * mm, "end": v(35.33, 29.32) * mm});
            skSolve(sketch);
        }
        {
            var Q0;
            Q0=makeQuery(id+"F4.imprint","IMPRINT",FACE,{"disambiguationData":[TD([[makeQuery(id+"F4.imprint","IMPRINT",EDGE,{"derivedFrom":sQuery(id+"F4.wireOp",EDGE,"E207.bottom")}),-1.0]])]});
            extrude(context, id + "F5", {"entities" : qUnion([Q0]), "endBound" : BoundingType.SYMMETRIC, "depth" : 130 * mm, "offsetDistance" : 25 * mm});
        }
        {
            var Q0;
            Q0=qCreatedBy(makeId("Top.planeOp"),FACE);
            var sketch = newSketch(context, id + "F6", { "sketchPlane" : qUnion([Q0])});
            skCircle(sketch, "E309", {"center": v(-60.07, -20.8) * mm, "radius": 2.5 * mm});
            skLineSegment(sketch, "E310.bottom", {"start": v(-51.57, -30.8) * mm, "end": v(-55.97, -30.8) * mm});
            skLineSegment(sketch, "E310.top", {"start": v(-51.57, -10.8) * mm, "end": v(-55.97, -10.8) * mm});
            skLineSegment(sketch, "E310.left", {"start": v(-50.07, -29.3) * mm, "end": v(-50.07, -24.4) * mm});
            skLineSegment(sketch, "E311.bottom", {"start": v(-58.05, -24.7) * mm, "end": v(-62.08, -24.7) * mm});
            skLineSegment(sketch, "E311.top", {"start": v(-58.05, -16.9) * mm, "end": v(-62.08, -16.9) * mm});
            skLineSegment(sketch, "E311.left", {"start": v(-56.17, -22.82) * mm, "end": v(-56.17, -18.8) * mm});
            skLineSegment(sketch, "E311.right", {"start": v(-63.97, -22.82) * mm, "end": v(-63.97, -18.8) * mm});
            skLineSegment(sketch, "E312.bottom", {"start": v(-51.57, -10.8) * mm, "end": v(-54.57, -10.8) * mm});
            skLineSegment(sketch, "E312.left", {"start": v(-50.07, -12.3) * mm, "end": v(-50.07, -15.3) * mm});
            skLineSegment(sketch, "E312.right", {"start": v(-54.57, -12.6) * mm, "end": v(-54.57, -14.25) * mm});
            skLineSegment(sketch, "E313", {"start": v(-55.58, -17.38) * mm, "end": v(-53.5, -15.3) * mm});
            skLineSegment(sketch, "E314.MirrorCS", {"start": v(-56.64, -16.32) * mm, "end": v(-54.57, -14.25) * mm});
            skLineSegment(sketch, "E315", {"start": v(-51.87, -15.3) * mm, "end": v(-51.87, -17.7) * mm});
            skLineSegment(sketch, "E316", {"start": v(-50.37, -17.2) * mm, "end": v(-50.07, -17.2) * mm});
            skLineSegment(sketch, "E317", {"start": v(-51.87, -17.7) * mm, "end": v(-50.57, -17.7) * mm});
            skLineSegment(sketch, "E318", {"start": v(-50.57, -17.4) * mm, "end": v(-50.57, -17.7) * mm});
            skPoint(sketch, "E319.visualSharp", {"position": v(-50.57, -17.2) * mm});
            skArc(sketch, "E319.filletArc", {"start": v(-50.37, -17.2) * mm, "mid": v(-50.5, -17.27) * mm, "end": v(-50.57, -17.4) * mm});
            skPoint(sketch, "E320.newPointA", {"position": v(-56.17, -17.97) * mm});
            skArc(sketch, "E320.filletArc", {"start": v(-55.58, -17.38) * mm, "mid": v(-56.01, -18.03) * mm, "end": v(-56.17, -18.8) * mm});
            skPoint(sketch, "E321.newPointA", {"position": v(-57.23, -16.9) * mm});
            skPoint(sketch, "E321.newPointB", {"position": v(-56.17, -16.9) * mm});
            skArc(sketch, "E321.filletArc", {"start": v(-58.05, -16.9) * mm, "mid": v(-57.29, -16.76) * mm, "end": v(-56.64, -16.32) * mm});
            skLineSegment(sketch, "E322.MirrorCS", {"start": v(-54.57, -12.6) * mm, "end": v(-56.97, -12.6) * mm});
            skLineSegment(sketch, "E323.MirrorCS", {"start": v(-56.97, -12.6) * mm, "end": v(-56.97, -11.3) * mm});
            skPoint(sketch, "E324.visualSharp", {"position": v(-50.07, -10.8) * mm});
            skArc(sketch, "E324.filletArc", {"start": v(-50.07, -12.3) * mm, "mid": v(-50.5, -11.25) * mm, "end": v(-51.57, -10.8) * mm});
            skLineSegment(sketch, "E325.trimOffspring", {"start": v(-51.87, -15.3) * mm, "end": v(-53.5, -15.3) * mm});
            skLineSegment(sketch, "E326.MirrorCS", {"start": v(-50.37, -24.4) * mm, "end": v(-50.07, -24.4) * mm});
            skArc(sketch, "E327.MirrorCS", {"start": v(-50.37, -24.4) * mm, "mid": v(-50.5, -24.35) * mm, "end": v(-50.57, -24.2) * mm});
            skLineSegment(sketch, "E328.MirrorCS", {"start": v(-50.57, -24.2) * mm, "end": v(-50.57, -23.9) * mm});
            skArc(sketch, "E329.MirrorCS", {"start": v(-55.58, -24.23) * mm, "mid": v(-56.01, -23.59) * mm, "end": v(-56.17, -22.82) * mm});
            skLineSegment(sketch, "E330.MirrorCS", {"start": v(-51.87, -26.3) * mm, "end": v(-53.5, -26.3) * mm});
            skLineSegment(sketch, "E331.MirrorCS", {"start": v(-51.87, -23.9) * mm, "end": v(-50.57, -23.9) * mm});
            skLineSegment(sketch, "E332.MirrorCS", {"start": v(-51.57, -30.8) * mm, "end": v(-54.57, -30.8) * mm});
            skPoint(sketch, "E333.MirrorP", {"position": v(-50.57, -24.4) * mm});
            skLineSegment(sketch, "E334.MirrorCS", {"start": v(-56.97, -29) * mm, "end": v(-56.97, -30.3) * mm});
            skLineSegment(sketch, "E335.MirrorCS", {"start": v(-54.57, -29) * mm, "end": v(-56.97, -29) * mm});
            skLineSegment(sketch, "E336.MirrorCS", {"start": v(-51.87, -26.3) * mm, "end": v(-51.87, -23.9) * mm});
            skLineSegment(sketch, "E337.MirrorCS", {"start": v(-50.07, -29.3) * mm, "end": v(-50.07, -26.3) * mm});
            skLineSegment(sketch, "E338.MirrorCS", {"start": v(-55.58, -24.23) * mm, "end": v(-53.5, -26.3) * mm});
            skPoint(sketch, "E339.MirrorP", {"position": v(-56.17, -23.65) * mm});
            skPoint(sketch, "E340.MirrorP", {"position": v(-50.07, -30.8) * mm});
            skPoint(sketch, "E341.MirrorP", {"position": v(-56.17, -24.7) * mm});
            skLineSegment(sketch, "E342.MirrorCS", {"start": v(-56.64, -25.3) * mm, "end": v(-54.57, -27.37) * mm});
            skPoint(sketch, "E343.MirrorP", {"position": v(-57.23, -24.7) * mm});
            skArc(sketch, "E344.MirrorCS", {"start": v(-50.07, -29.3) * mm, "mid": v(-50.5, -30.37) * mm, "end": v(-51.57, -30.8) * mm});
            skLineSegment(sketch, "E345.MirrorCS", {"start": v(-54.57, -29) * mm, "end": v(-54.57, -27.37) * mm});
            skArc(sketch, "E346.MirrorCS", {"start": v(-58.05, -24.7) * mm, "mid": v(-57.29, -24.86) * mm, "end": v(-56.64, -25.3) * mm});
            skLineSegment(sketch, "E347.trimOffspring", {"start": v(-50.07, -17.2) * mm, "end": v(-50.07, -12.3) * mm});
            skLineSegment(sketch, "E348.MirrorCS", {"start": v(-56.47, -11.1) * mm, "end": v(-56.47, -10.8) * mm});
            skArc(sketch, "E349.MirrorCS", {"start": v(-56.47, -11.1) * mm, "mid": v(-56.52, -11.25) * mm, "end": v(-56.67, -11.3) * mm});
            skLineSegment(sketch, "E350.MirrorCS", {"start": v(-56.67, -11.3) * mm, "end": v(-56.97, -11.3) * mm});
            skLineSegment(sketch, "E351", {"start": v(-55.97, -10.8) * mm, "end": v(-56.47, -10.8) * mm});
            skLineSegment(sketch, "E352.MirrorCS", {"start": v(-56.47, -30.5) * mm, "end": v(-56.47, -30.8) * mm});
            skLineSegment(sketch, "E353.MirrorCS", {"start": v(-56.67, -30.3) * mm, "end": v(-56.97, -30.3) * mm});
            skLineSegment(sketch, "E354.MirrorCS", {"start": v(-55.97, -30.8) * mm, "end": v(-56.47, -30.8) * mm});
            skArc(sketch, "E355.MirrorCS", {"start": v(-56.47, -30.5) * mm, "mid": v(-56.52, -30.37) * mm, "end": v(-56.67, -30.3) * mm});
            skArc(sketch, "E356.MirrorCS", {"start": v(-69.77, -24.4) * mm, "mid": v(-69.62, -24.35) * mm, "end": v(-69.57, -24.2) * mm});
            skLineSegment(sketch, "E357.MirrorCS", {"start": v(-69.77, -17.2) * mm, "end": v(-70.07, -17.2) * mm});
            skLineSegment(sketch, "E358.MirrorCS", {"start": v(-69.57, -24.2) * mm, "end": v(-69.57, -23.9) * mm});
            skArc(sketch, "E359.MirrorCS", {"start": v(-69.77, -17.2) * mm, "mid": v(-69.62, -17.27) * mm, "end": v(-69.57, -17.4) * mm});
            skLineSegment(sketch, "E360.MirrorCS", {"start": v(-69.57, -17.4) * mm, "end": v(-69.57, -17.7) * mm});
            skLineSegment(sketch, "E361.MirrorCS", {"start": v(-69.77, -24.4) * mm, "end": v(-70.07, -24.4) * mm});
            skLineSegment(sketch, "E362.MirrorCS", {"start": v(-64.17, -10.8) * mm, "end": v(-63.67, -10.8) * mm});
            skArc(sketch, "E363.MirrorCS", {"start": v(-70.07, -29.3) * mm, "mid": v(-69.63, -30.37) * mm, "end": v(-68.57, -30.8) * mm});
            skLineSegment(sketch, "E364.MirrorCS", {"start": v(-63.67, -11.1) * mm, "end": v(-63.67, -10.8) * mm});
            skArc(sketch, "E365.MirrorCS", {"start": v(-64.55, -17.38) * mm, "mid": v(-64.12, -18.03) * mm, "end": v(-63.97, -18.8) * mm});
            skLineSegment(sketch, "E366.MirrorCS", {"start": v(-63.47, -30.3) * mm, "end": v(-63.17, -30.3) * mm});
            skLineSegment(sketch, "E367.MirrorCS", {"start": v(-63.17, -12.6) * mm, "end": v(-63.17, -11.3) * mm});
            skLineSegment(sketch, "E368.MirrorCS", {"start": v(-62.08, -16.9) * mm, "end": v(-58.05, -16.9) * mm});
            skLineSegment(sketch, "E369.MirrorCS", {"start": v(-68.27, -23.9) * mm, "end": v(-69.57, -23.9) * mm});
            skLineSegment(sketch, "E370.MirrorCS", {"start": v(-68.27, -17.7) * mm, "end": v(-69.57, -17.7) * mm});
            skLineSegment(sketch, "E371.MirrorCS", {"start": v(-63.47, -11.3) * mm, "end": v(-63.17, -11.3) * mm});
            skArc(sketch, "E372.MirrorCS", {"start": v(-64.55, -24.23) * mm, "mid": v(-64.12, -23.59) * mm, "end": v(-63.97, -22.82) * mm});
            skArc(sketch, "E373.MirrorCS", {"start": v(-63.67, -30.5) * mm, "mid": v(-63.6, -30.37) * mm, "end": v(-63.47, -30.3) * mm});
            skArc(sketch, "E374.MirrorCS", {"start": v(-63.67, -11.1) * mm, "mid": v(-63.6, -11.25) * mm, "end": v(-63.47, -11.3) * mm});
            skLineSegment(sketch, "E375.MirrorCS", {"start": v(-63.67, -30.5) * mm, "end": v(-63.67, -30.8) * mm});
            skLineSegment(sketch, "E376.MirrorCS", {"start": v(-62.08, -24.7) * mm, "end": v(-58.05, -24.7) * mm});
            skLineSegment(sketch, "E377.MirrorCS", {"start": v(-64.17, -30.8) * mm, "end": v(-63.67, -30.8) * mm});
            skLineSegment(sketch, "E378.MirrorCS", {"start": v(-63.17, -29) * mm, "end": v(-63.17, -30.3) * mm});
            skArc(sketch, "E379.MirrorCS", {"start": v(-62.08, -16.9) * mm, "mid": v(-62.84, -16.76) * mm, "end": v(-63.5, -16.32) * mm});
            skPoint(sketch, "E380.MirrorP", {"position": v(-70.07, -30.8) * mm});
            skLineSegment(sketch, "E381.MirrorCS", {"start": v(-68.57, -30.8) * mm, "end": v(-64.17, -30.8) * mm});
            skPoint(sketch, "E382.MirrorP", {"position": v(-63.97, -24.7) * mm});
            skLineSegment(sketch, "E383.MirrorCS", {"start": v(-68.57, -10.8) * mm, "end": v(-64.17, -10.8) * mm});
            skArc(sketch, "E384.MirrorCS", {"start": v(-62.08, -24.7) * mm, "mid": v(-62.84, -24.86) * mm, "end": v(-63.5, -25.3) * mm});
            skArc(sketch, "E385.MirrorCS", {"start": v(-70.07, -12.3) * mm, "mid": v(-69.63, -11.25) * mm, "end": v(-68.57, -10.8) * mm});
            skPoint(sketch, "E386.MirrorP", {"position": v(-63.97, -23.65) * mm});
            skLineSegment(sketch, "E387.MirrorCS", {"start": v(-65.57, -12.6) * mm, "end": v(-65.57, -14.25) * mm});
            skLineSegment(sketch, "E388.MirrorCS", {"start": v(-63.5, -16.32) * mm, "end": v(-65.57, -14.25) * mm});
            skPoint(sketch, "E389.MirrorP", {"position": v(-63.97, -17.97) * mm});
            skLineSegment(sketch, "E390.MirrorCS", {"start": v(-68.27, -26.3) * mm, "end": v(-68.27, -23.9) * mm});
            skLineSegment(sketch, "E391.MirrorCS", {"start": v(-64.55, -24.23) * mm, "end": v(-66.63, -26.3) * mm});
            skLineSegment(sketch, "E392.MirrorCS", {"start": v(-65.57, -29) * mm, "end": v(-63.17, -29) * mm});
            skLineSegment(sketch, "E393.MirrorCS", {"start": v(-68.27, -26.3) * mm, "end": v(-66.63, -26.3) * mm});
            skLineSegment(sketch, "E394.MirrorCS", {"start": v(-70.07, -29.3) * mm, "end": v(-70.07, -26.3) * mm});
            skLineSegment(sketch, "E395.MirrorCS", {"start": v(-68.57, -10.8) * mm, "end": v(-65.57, -10.8) * mm});
            skLineSegment(sketch, "E396.MirrorCS", {"start": v(-70.07, -17.2) * mm, "end": v(-70.07, -12.3) * mm});
            skLineSegment(sketch, "E397.MirrorCS", {"start": v(-65.57, -12.6) * mm, "end": v(-63.17, -12.6) * mm});
            skLineSegment(sketch, "E398.MirrorCS", {"start": v(-63.5, -25.3) * mm, "end": v(-65.57, -27.37) * mm});
            skPoint(sketch, "E399.MirrorP", {"position": v(-62.9, -24.7) * mm});
            skLineSegment(sketch, "E400.MirrorCS", {"start": v(-68.27, -15.3) * mm, "end": v(-68.27, -17.7) * mm});
            skLineSegment(sketch, "E401.MirrorCS", {"start": v(-70.07, -12.3) * mm, "end": v(-70.07, -15.3) * mm});
            skPoint(sketch, "E402.MirrorP", {"position": v(-69.57, -24.4) * mm});
            skPoint(sketch, "E403.MirrorP", {"position": v(-70.07, -10.8) * mm});
            skPoint(sketch, "E404.MirrorP", {"position": v(-69.57, -17.2) * mm});
            skLineSegment(sketch, "E405.MirrorCS", {"start": v(-64.55, -17.38) * mm, "end": v(-66.63, -15.3) * mm});
            skLineSegment(sketch, "E406.MirrorCS", {"start": v(-68.27, -15.3) * mm, "end": v(-66.63, -15.3) * mm});
            skLineSegment(sketch, "E407.MirrorCS", {"start": v(-70.07, -29.3) * mm, "end": v(-70.07, -24.4) * mm});
            skLineSegment(sketch, "E408.MirrorCS", {"start": v(-68.57, -30.8) * mm, "end": v(-65.57, -30.8) * mm});
            skPoint(sketch, "E409.MirrorP", {"position": v(-63.97, -16.9) * mm});
            skPoint(sketch, "E410.MirrorP", {"position": v(-62.9, -16.9) * mm});
            skLineSegment(sketch, "E411.MirrorCS", {"start": v(-65.57, -29) * mm, "end": v(-65.57, -27.37) * mm});
            skSolve(sketch);
        }
        {
            var Q0;
            Q0=makeQuery(id+"F6.imprint","IMPRINT",FACE,{"disambiguationData":[TD([[makeQuery(id+"F6.imprint","IMPRINT",EDGE,{"derivedFrom":sQuery(id+"F6.wireOp",EDGE,"E310.bottom")}),-1.0]])]});
            extrude(context, id + "F7", {"entities" : qUnion([Q0]), "endBound" : BoundingType.SYMMETRIC, "depth" : 400 * mm, "offsetDistance" : 25 * mm});
        }
        {
            var Q0;
            Q0=qCreatedBy(makeId("Top.planeOp"),FACE);
            var sketch = newSketch(context, id + "F8", { "sketchPlane" : qUnion([Q0])});
            skCircle(sketch, "E412", {"center": v(-65.76, 48.88) * mm, "radius": 2.5 * mm});
            skLineSegment(sketch, "E413.bottom", {"start": v(-57.26, 38.88) * mm, "end": v(-61.66, 38.88) * mm});
            skLineSegment(sketch, "E413.top", {"start": v(-57.26, 58.88) * mm, "end": v(-61.66, 58.88) * mm});
            skLineSegment(sketch, "E413.left", {"start": v(-55.76, 40.38) * mm, "end": v(-55.76, 45.28) * mm});
            skLineSegment(sketch, "E414.bottom", {"start": v(-63.75, 44.98) * mm, "end": v(-67.77, 44.98) * mm});
            skLineSegment(sketch, "E414.top", {"start": v(-63.75, 52.78) * mm, "end": v(-67.77, 52.78) * mm});
            skLineSegment(sketch, "E414.left", {"start": v(-61.86, 46.87) * mm, "end": v(-61.86, 50.9) * mm});
            skLineSegment(sketch, "E414.right", {"start": v(-69.66, 46.87) * mm, "end": v(-69.66, 50.9) * mm});
            skLineSegment(sketch, "E415.bottom", {"start": v(-57.26, 58.88) * mm, "end": v(-60.26, 58.88) * mm});
            skLineSegment(sketch, "E415.left", {"start": v(-55.76, 57.38) * mm, "end": v(-55.76, 54.38) * mm});
            skLineSegment(sketch, "E415.right", {"start": v(-60.26, 57.08) * mm, "end": v(-60.26, 55.44) * mm});
            skLineSegment(sketch, "E416", {"start": v(-61.27, 52.3) * mm, "end": v(-59.2, 54.38) * mm});
            skLineSegment(sketch, "E417.MirrorCS", {"start": v(-62.33, 53.37) * mm, "end": v(-60.26, 55.44) * mm});
            skLineSegment(sketch, "E418", {"start": v(-57.56, 54.38) * mm, "end": v(-57.56, 51.98) * mm});
            skLineSegment(sketch, "E419", {"start": v(-56.06, 52.48) * mm, "end": v(-55.76, 52.48) * mm});
            skLineSegment(sketch, "E420", {"start": v(-57.56, 51.98) * mm, "end": v(-56.26, 51.98) * mm});
            skLineSegment(sketch, "E421", {"start": v(-56.26, 52.28) * mm, "end": v(-56.26, 51.98) * mm});
            skPoint(sketch, "E422.visualSharp", {"position": v(-56.26, 52.48) * mm});
            skArc(sketch, "E422.filletArc", {"start": v(-56.06, 52.48) * mm, "mid": v(-56.2, 52.42) * mm, "end": v(-56.26, 52.28) * mm});
            skPoint(sketch, "E423.newPointA", {"position": v(-61.86, 51.72) * mm});
            skArc(sketch, "E423.filletArc", {"start": v(-61.27, 52.3) * mm, "mid": v(-61.7, 51.66) * mm, "end": v(-61.86, 50.9) * mm});
            skPoint(sketch, "E424.newPointA", {"position": v(-62.92, 52.78) * mm});
            skPoint(sketch, "E424.newPointB", {"position": v(-61.86, 52.78) * mm});
            skArc(sketch, "E424.filletArc", {"start": v(-63.75, 52.78) * mm, "mid": v(-62.98, 52.93) * mm, "end": v(-62.33, 53.37) * mm});
            skLineSegment(sketch, "E425.MirrorCS", {"start": v(-60.26, 57.08) * mm, "end": v(-62.66, 57.08) * mm});
            skLineSegment(sketch, "E426.MirrorCS", {"start": v(-62.66, 57.08) * mm, "end": v(-62.66, 58.38) * mm});
            skPoint(sketch, "E427.visualSharp", {"position": v(-55.76, 58.88) * mm});
            skArc(sketch, "E427.filletArc", {"start": v(-55.76, 57.38) * mm, "mid": v(-56.2, 58.44) * mm, "end": v(-57.26, 58.88) * mm});
            skLineSegment(sketch, "E428.trimOffspring", {"start": v(-57.56, 54.38) * mm, "end": v(-59.2, 54.38) * mm});
            skLineSegment(sketch, "E429.MirrorCS", {"start": v(-56.06, 45.28) * mm, "end": v(-55.76, 45.28) * mm});
            skArc(sketch, "E430.MirrorCS", {"start": v(-56.06, 45.28) * mm, "mid": v(-56.2, 45.34) * mm, "end": v(-56.26, 45.48) * mm});
            skLineSegment(sketch, "E431.MirrorCS", {"start": v(-56.26, 45.48) * mm, "end": v(-56.26, 45.78) * mm});
            skArc(sketch, "E432.MirrorCS", {"start": v(-61.27, 45.45) * mm, "mid": v(-61.7, 46.1) * mm, "end": v(-61.86, 46.87) * mm});
            skLineSegment(sketch, "E433.MirrorCS", {"start": v(-57.56, 43.38) * mm, "end": v(-59.2, 43.38) * mm});
            skLineSegment(sketch, "E434.MirrorCS", {"start": v(-57.56, 45.78) * mm, "end": v(-56.26, 45.78) * mm});
            skLineSegment(sketch, "E435.MirrorCS", {"start": v(-57.26, 38.88) * mm, "end": v(-60.26, 38.88) * mm});
            skPoint(sketch, "E436.MirrorP", {"position": v(-56.26, 45.28) * mm});
            skLineSegment(sketch, "E437.MirrorCS", {"start": v(-62.66, 40.68) * mm, "end": v(-62.66, 39.38) * mm});
            skLineSegment(sketch, "E438.MirrorCS", {"start": v(-60.26, 40.68) * mm, "end": v(-62.66, 40.68) * mm});
            skLineSegment(sketch, "E439.MirrorCS", {"start": v(-57.56, 43.38) * mm, "end": v(-57.56, 45.78) * mm});
            skLineSegment(sketch, "E440.MirrorCS", {"start": v(-55.76, 40.38) * mm, "end": v(-55.76, 43.38) * mm});
            skLineSegment(sketch, "E441.MirrorCS", {"start": v(-61.27, 45.45) * mm, "end": v(-59.2, 43.38) * mm});
            skPoint(sketch, "E442.MirrorP", {"position": v(-61.86, 46.04) * mm});
            skPoint(sketch, "E443.MirrorP", {"position": v(-55.76, 38.88) * mm});
            skPoint(sketch, "E444.MirrorP", {"position": v(-61.86, 44.98) * mm});
            skLineSegment(sketch, "E445.MirrorCS", {"start": v(-62.33, 44.4) * mm, "end": v(-60.26, 42.32) * mm});
            skPoint(sketch, "E446.MirrorP", {"position": v(-62.92, 44.98) * mm});
            skArc(sketch, "E447.MirrorCS", {"start": v(-55.76, 40.38) * mm, "mid": v(-56.2, 39.32) * mm, "end": v(-57.26, 38.88) * mm});
            skLineSegment(sketch, "E448.MirrorCS", {"start": v(-60.26, 40.68) * mm, "end": v(-60.26, 42.32) * mm});
            skArc(sketch, "E449.MirrorCS", {"start": v(-63.75, 44.98) * mm, "mid": v(-62.98, 44.83) * mm, "end": v(-62.33, 44.4) * mm});
            skLineSegment(sketch, "E450.trimOffspring", {"start": v(-55.76, 52.48) * mm, "end": v(-55.76, 57.38) * mm});
            skLineSegment(sketch, "E451.MirrorCS", {"start": v(-62.16, 58.58) * mm, "end": v(-62.16, 58.88) * mm});
            skArc(sketch, "E452.MirrorCS", {"start": v(-62.16, 58.58) * mm, "mid": v(-62.22, 58.44) * mm, "end": v(-62.36, 58.38) * mm});
            skLineSegment(sketch, "E453.MirrorCS", {"start": v(-62.36, 58.38) * mm, "end": v(-62.66, 58.38) * mm});
            skLineSegment(sketch, "E454", {"start": v(-61.66, 58.88) * mm, "end": v(-62.16, 58.88) * mm});
            skLineSegment(sketch, "E455.MirrorCS", {"start": v(-62.16, 39.18) * mm, "end": v(-62.16, 38.88) * mm});
            skLineSegment(sketch, "E456.MirrorCS", {"start": v(-62.36, 39.38) * mm, "end": v(-62.66, 39.38) * mm});
            skLineSegment(sketch, "E457.MirrorCS", {"start": v(-61.66, 38.88) * mm, "end": v(-62.16, 38.88) * mm});
            skArc(sketch, "E458.MirrorCS", {"start": v(-62.16, 39.18) * mm, "mid": v(-62.22, 39.32) * mm, "end": v(-62.36, 39.38) * mm});
            skArc(sketch, "E459.MirrorCS", {"start": v(-75.46, 45.28) * mm, "mid": v(-75.32, 45.34) * mm, "end": v(-75.26, 45.48) * mm});
            skLineSegment(sketch, "E460.MirrorCS", {"start": v(-75.46, 52.48) * mm, "end": v(-75.76, 52.48) * mm});
            skLineSegment(sketch, "E461.MirrorCS", {"start": v(-75.26, 45.48) * mm, "end": v(-75.26, 45.78) * mm});
            skArc(sketch, "E462.MirrorCS", {"start": v(-75.46, 52.48) * mm, "mid": v(-75.32, 52.42) * mm, "end": v(-75.26, 52.28) * mm});
            skLineSegment(sketch, "E463.MirrorCS", {"start": v(-75.26, 52.28) * mm, "end": v(-75.26, 51.98) * mm});
            skLineSegment(sketch, "E464.MirrorCS", {"start": v(-75.46, 45.28) * mm, "end": v(-75.76, 45.28) * mm});
            skLineSegment(sketch, "E465.MirrorCS", {"start": v(-69.86, 58.88) * mm, "end": v(-69.36, 58.88) * mm});
            skArc(sketch, "E466.MirrorCS", {"start": v(-75.76, 40.38) * mm, "mid": v(-75.32, 39.32) * mm, "end": v(-74.26, 38.88) * mm});
            skLineSegment(sketch, "E467.MirrorCS", {"start": v(-69.36, 58.58) * mm, "end": v(-69.36, 58.88) * mm});
            skArc(sketch, "E468.MirrorCS", {"start": v(-70.24, 52.3) * mm, "mid": v(-69.81, 51.66) * mm, "end": v(-69.66, 50.9) * mm});
            skLineSegment(sketch, "E469.MirrorCS", {"start": v(-69.16, 39.38) * mm, "end": v(-68.86, 39.38) * mm});
            skLineSegment(sketch, "E470.MirrorCS", {"start": v(-68.86, 57.08) * mm, "end": v(-68.86, 58.38) * mm});
            skLineSegment(sketch, "E471.MirrorCS", {"start": v(-67.77, 52.78) * mm, "end": v(-63.75, 52.78) * mm});
            skLineSegment(sketch, "E472.MirrorCS", {"start": v(-73.96, 45.78) * mm, "end": v(-75.26, 45.78) * mm});
            skLineSegment(sketch, "E473.MirrorCS", {"start": v(-73.96, 51.98) * mm, "end": v(-75.26, 51.98) * mm});
            skLineSegment(sketch, "E474.MirrorCS", {"start": v(-69.16, 58.38) * mm, "end": v(-68.86, 58.38) * mm});
            skArc(sketch, "E475.MirrorCS", {"start": v(-70.24, 45.45) * mm, "mid": v(-69.81, 46.1) * mm, "end": v(-69.66, 46.87) * mm});
            skArc(sketch, "E476.MirrorCS", {"start": v(-69.36, 39.18) * mm, "mid": v(-69.3, 39.32) * mm, "end": v(-69.16, 39.38) * mm});
            skArc(sketch, "E477.MirrorCS", {"start": v(-69.36, 58.58) * mm, "mid": v(-69.3, 58.44) * mm, "end": v(-69.16, 58.38) * mm});
            skLineSegment(sketch, "E478.MirrorCS", {"start": v(-69.36, 39.18) * mm, "end": v(-69.36, 38.88) * mm});
            skLineSegment(sketch, "E479.MirrorCS", {"start": v(-67.77, 44.98) * mm, "end": v(-63.75, 44.98) * mm});
            skLineSegment(sketch, "E480.MirrorCS", {"start": v(-69.86, 38.88) * mm, "end": v(-69.36, 38.88) * mm});
            skLineSegment(sketch, "E481.MirrorCS", {"start": v(-68.86, 40.68) * mm, "end": v(-68.86, 39.38) * mm});
            skArc(sketch, "E482.MirrorCS", {"start": v(-67.77, 52.78) * mm, "mid": v(-68.54, 52.93) * mm, "end": v(-69.18, 53.37) * mm});
            skPoint(sketch, "E483.MirrorP", {"position": v(-75.76, 38.88) * mm});
            skLineSegment(sketch, "E484.MirrorCS", {"start": v(-74.26, 38.88) * mm, "end": v(-69.86, 38.88) * mm});
            skPoint(sketch, "E485.MirrorP", {"position": v(-69.66, 44.98) * mm});
            skLineSegment(sketch, "E486.MirrorCS", {"start": v(-74.26, 58.88) * mm, "end": v(-69.86, 58.88) * mm});
            skArc(sketch, "E487.MirrorCS", {"start": v(-67.77, 44.98) * mm, "mid": v(-68.54, 44.83) * mm, "end": v(-69.18, 44.4) * mm});
            skArc(sketch, "E488.MirrorCS", {"start": v(-75.76, 57.38) * mm, "mid": v(-75.32, 58.44) * mm, "end": v(-74.26, 58.88) * mm});
            skPoint(sketch, "E489.MirrorP", {"position": v(-69.66, 46.04) * mm});
            skLineSegment(sketch, "E490.MirrorCS", {"start": v(-71.26, 57.08) * mm, "end": v(-71.26, 55.44) * mm});
            skLineSegment(sketch, "E491.MirrorCS", {"start": v(-69.18, 53.37) * mm, "end": v(-71.26, 55.44) * mm});
            skPoint(sketch, "E492.MirrorP", {"position": v(-69.66, 51.72) * mm});
            skLineSegment(sketch, "E493.MirrorCS", {"start": v(-73.96, 43.38) * mm, "end": v(-73.96, 45.78) * mm});
            skLineSegment(sketch, "E494.MirrorCS", {"start": v(-70.24, 45.45) * mm, "end": v(-72.32, 43.38) * mm});
            skLineSegment(sketch, "E495.MirrorCS", {"start": v(-71.26, 40.68) * mm, "end": v(-68.86, 40.68) * mm});
            skLineSegment(sketch, "E496.MirrorCS", {"start": v(-73.96, 43.38) * mm, "end": v(-72.32, 43.38) * mm});
            skLineSegment(sketch, "E497.MirrorCS", {"start": v(-75.76, 40.38) * mm, "end": v(-75.76, 43.38) * mm});
            skLineSegment(sketch, "E498.MirrorCS", {"start": v(-74.26, 58.88) * mm, "end": v(-71.26, 58.88) * mm});
            skLineSegment(sketch, "E499.MirrorCS", {"start": v(-75.76, 52.48) * mm, "end": v(-75.76, 57.38) * mm});
            skLineSegment(sketch, "E500.MirrorCS", {"start": v(-71.26, 57.08) * mm, "end": v(-68.86, 57.08) * mm});
            skLineSegment(sketch, "E501.MirrorCS", {"start": v(-69.18, 44.4) * mm, "end": v(-71.26, 42.32) * mm});
            skPoint(sketch, "E502.MirrorP", {"position": v(-68.6, 44.98) * mm});
            skLineSegment(sketch, "E503.MirrorCS", {"start": v(-73.96, 54.38) * mm, "end": v(-73.96, 51.98) * mm});
            skLineSegment(sketch, "E504.MirrorCS", {"start": v(-75.76, 57.38) * mm, "end": v(-75.76, 54.38) * mm});
            skPoint(sketch, "E505.MirrorP", {"position": v(-75.26, 45.28) * mm});
            skPoint(sketch, "E506.MirrorP", {"position": v(-75.76, 58.88) * mm});
            skPoint(sketch, "E507.MirrorP", {"position": v(-75.26, 52.48) * mm});
            skLineSegment(sketch, "E508.MirrorCS", {"start": v(-70.24, 52.3) * mm, "end": v(-72.32, 54.38) * mm});
            skLineSegment(sketch, "E509.MirrorCS", {"start": v(-73.96, 54.38) * mm, "end": v(-72.32, 54.38) * mm});
            skLineSegment(sketch, "E510.MirrorCS", {"start": v(-75.76, 40.38) * mm, "end": v(-75.76, 45.28) * mm});
            skLineSegment(sketch, "E511.MirrorCS", {"start": v(-74.26, 38.88) * mm, "end": v(-71.26, 38.88) * mm});
            skPoint(sketch, "E512.MirrorP", {"position": v(-69.66, 52.78) * mm});
            skPoint(sketch, "E513.MirrorP", {"position": v(-68.6, 52.78) * mm});
            skLineSegment(sketch, "E514.MirrorCS", {"start": v(-71.26, 40.68) * mm, "end": v(-71.26, 42.32) * mm});
            skSolve(sketch);
        }
        {
            var Q0;
            Q0=makeQuery(id+"F8.imprint","IMPRINT",FACE,{"disambiguationData":[TD([[makeQuery(id+"F8.imprint","IMPRINT",EDGE,{"derivedFrom":sQuery(id+"F8.wireOp",EDGE,"E413.bottom")}),-1.0]])]});
            extrude(context, id + "F9", {"entities" : qUnion([Q0]), "endBound" : BoundingType.SYMMETRIC, "depth" : 80 * mm, "offsetDistance" : 25 * mm});
        }
        {
            var Q0;
            Q0=qCreatedBy(makeId("Top.planeOp"),FACE);
            var sketch = newSketch(context, id + "F10", { "sketchPlane" : qUnion([Q0])});
            skCircle(sketch, "E515", {"center": v(122.33, -21.93) * mm, "radius": 2.5 * mm});
            skLineSegment(sketch, "E516.bottom", {"start": v(130.83, -31.93) * mm, "end": v(126.43, -31.93) * mm});
            skLineSegment(sketch, "E516.top", {"start": v(130.83, -11.93) * mm, "end": v(126.43, -11.93) * mm});
            skLineSegment(sketch, "E516.left", {"start": v(132.33, -30.43) * mm, "end": v(132.33, -25.53) * mm});
            skLineSegment(sketch, "E517.bottom", {"start": v(124.34, -25.83) * mm, "end": v(120.32, -25.83) * mm});
            skLineSegment(sketch, "E517.top", {"start": v(124.34, -18.03) * mm, "end": v(120.32, -18.03) * mm});
            skLineSegment(sketch, "E517.left", {"start": v(126.23, -23.94) * mm, "end": v(126.23, -19.92) * mm});
            skLineSegment(sketch, "E517.right", {"start": v(118.43, -23.94) * mm, "end": v(118.43, -19.92) * mm});
            skLineSegment(sketch, "E518.bottom", {"start": v(130.83, -11.93) * mm, "end": v(127.83, -11.93) * mm});
            skLineSegment(sketch, "E518.left", {"start": v(132.33, -13.43) * mm, "end": v(132.33, -16.43) * mm});
            skLineSegment(sketch, "E518.right", {"start": v(127.83, -13.73) * mm, "end": v(127.83, -15.37) * mm});
            skLineSegment(sketch, "E519", {"start": v(126.81, -18.5) * mm, "end": v(128.89, -16.43) * mm});
            skLineSegment(sketch, "E520.MirrorCS", {"start": v(125.75, -17.44) * mm, "end": v(127.83, -15.37) * mm});
            skLineSegment(sketch, "E521", {"start": v(130.53, -16.43) * mm, "end": v(130.53, -18.83) * mm});
            skLineSegment(sketch, "E522", {"start": v(132.03, -18.33) * mm, "end": v(132.33, -18.33) * mm});
            skLineSegment(sketch, "E523", {"start": v(130.53, -18.83) * mm, "end": v(131.83, -18.83) * mm});
            skLineSegment(sketch, "E524", {"start": v(131.83, -18.53) * mm, "end": v(131.83, -18.83) * mm});
            skPoint(sketch, "E525.visualSharp", {"position": v(131.83, -18.33) * mm});
            skArc(sketch, "E525.filletArc", {"start": v(132.03, -18.33) * mm, "mid": v(131.89, -18.39) * mm, "end": v(131.83, -18.53) * mm});
            skPoint(sketch, "E526.newPointA", {"position": v(126.23, -19.1) * mm});
            skArc(sketch, "E526.filletArc", {"start": v(126.81, -18.5) * mm, "mid": v(126.38, -19.15) * mm, "end": v(126.23, -19.92) * mm});
            skPoint(sketch, "E527.newPointA", {"position": v(125.17, -18.03) * mm});
            skPoint(sketch, "E527.newPointB", {"position": v(126.23, -18.03) * mm});
            skArc(sketch, "E527.filletArc", {"start": v(124.34, -18.03) * mm, "mid": v(125.1, -17.88) * mm, "end": v(125.75, -17.44) * mm});
            skLineSegment(sketch, "E528.MirrorCS", {"start": v(127.83, -13.73) * mm, "end": v(125.43, -13.73) * mm});
            skLineSegment(sketch, "E529.MirrorCS", {"start": v(125.43, -13.73) * mm, "end": v(125.43, -12.43) * mm});
            skPoint(sketch, "E530.visualSharp", {"position": v(132.33, -11.93) * mm});
            skArc(sketch, "E530.filletArc", {"start": v(132.33, -13.43) * mm, "mid": v(131.89, -12.37) * mm, "end": v(130.83, -11.93) * mm});
            skLineSegment(sketch, "E531.trimOffspring", {"start": v(130.53, -16.43) * mm, "end": v(128.89, -16.43) * mm});
            skLineSegment(sketch, "E532.MirrorCS", {"start": v(132.03, -25.53) * mm, "end": v(132.33, -25.53) * mm});
            skArc(sketch, "E533.MirrorCS", {"start": v(132.03, -25.53) * mm, "mid": v(131.89, -25.47) * mm, "end": v(131.83, -25.33) * mm});
            skLineSegment(sketch, "E534.MirrorCS", {"start": v(131.83, -25.33) * mm, "end": v(131.83, -25.03) * mm});
            skArc(sketch, "E535.MirrorCS", {"start": v(126.81, -25.35) * mm, "mid": v(126.38, -24.7) * mm, "end": v(126.23, -23.94) * mm});
            skLineSegment(sketch, "E536.MirrorCS", {"start": v(130.53, -27.43) * mm, "end": v(128.89, -27.43) * mm});
            skLineSegment(sketch, "E537.MirrorCS", {"start": v(130.53, -25.03) * mm, "end": v(131.83, -25.03) * mm});
            skLineSegment(sketch, "E538.MirrorCS", {"start": v(130.83, -31.93) * mm, "end": v(127.83, -31.93) * mm});
            skPoint(sketch, "E539.MirrorP", {"position": v(131.83, -25.53) * mm});
            skLineSegment(sketch, "E540.MirrorCS", {"start": v(125.43, -30.13) * mm, "end": v(125.43, -31.43) * mm});
            skLineSegment(sketch, "E541.MirrorCS", {"start": v(127.83, -30.13) * mm, "end": v(125.43, -30.13) * mm});
            skLineSegment(sketch, "E542.MirrorCS", {"start": v(130.53, -27.43) * mm, "end": v(130.53, -25.03) * mm});
            skLineSegment(sketch, "E543.MirrorCS", {"start": v(132.33, -30.43) * mm, "end": v(132.33, -27.43) * mm});
            skLineSegment(sketch, "E544.MirrorCS", {"start": v(126.81, -25.35) * mm, "end": v(128.89, -27.43) * mm});
            skPoint(sketch, "E545.MirrorP", {"position": v(126.23, -24.77) * mm});
            skPoint(sketch, "E546.MirrorP", {"position": v(132.33, -31.93) * mm});
            skPoint(sketch, "E547.MirrorP", {"position": v(126.23, -25.83) * mm});
            skLineSegment(sketch, "E548.MirrorCS", {"start": v(125.75, -26.42) * mm, "end": v(127.83, -28.5) * mm});
            skPoint(sketch, "E549.MirrorP", {"position": v(125.17, -25.83) * mm});
            skArc(sketch, "E550.MirrorCS", {"start": v(132.33, -30.43) * mm, "mid": v(131.89, -31.5) * mm, "end": v(130.83, -31.93) * mm});
            skLineSegment(sketch, "E551.MirrorCS", {"start": v(127.83, -30.13) * mm, "end": v(127.83, -28.5) * mm});
            skArc(sketch, "E552.MirrorCS", {"start": v(124.34, -25.83) * mm, "mid": v(125.1, -25.98) * mm, "end": v(125.75, -26.42) * mm});
            skLineSegment(sketch, "E553.trimOffspring", {"start": v(132.33, -18.33) * mm, "end": v(132.33, -13.43) * mm});
            skLineSegment(sketch, "E554.MirrorCS", {"start": v(125.93, -12.23) * mm, "end": v(125.93, -11.93) * mm});
            skArc(sketch, "E555.MirrorCS", {"start": v(125.93, -12.23) * mm, "mid": v(125.87, -12.37) * mm, "end": v(125.73, -12.43) * mm});
            skLineSegment(sketch, "E556.MirrorCS", {"start": v(125.73, -12.43) * mm, "end": v(125.43, -12.43) * mm});
            skLineSegment(sketch, "E557", {"start": v(126.43, -11.93) * mm, "end": v(125.93, -11.93) * mm});
            skLineSegment(sketch, "E558.MirrorCS", {"start": v(125.93, -31.63) * mm, "end": v(125.93, -31.93) * mm});
            skLineSegment(sketch, "E559.MirrorCS", {"start": v(125.73, -31.43) * mm, "end": v(125.43, -31.43) * mm});
            skLineSegment(sketch, "E560.MirrorCS", {"start": v(126.43, -31.93) * mm, "end": v(125.93, -31.93) * mm});
            skArc(sketch, "E561.MirrorCS", {"start": v(125.93, -31.63) * mm, "mid": v(125.87, -31.49) * mm, "end": v(125.73, -31.43) * mm});
            skArc(sketch, "E562.MirrorCS", {"start": v(112.63, -25.53) * mm, "mid": v(112.77, -25.47) * mm, "end": v(112.83, -25.33) * mm});
            skLineSegment(sketch, "E563.MirrorCS", {"start": v(112.63, -18.33) * mm, "end": v(112.33, -18.33) * mm});
            skLineSegment(sketch, "E564.MirrorCS", {"start": v(112.83, -25.33) * mm, "end": v(112.83, -25.03) * mm});
            skArc(sketch, "E565.MirrorCS", {"start": v(112.63, -18.33) * mm, "mid": v(112.77, -18.39) * mm, "end": v(112.83, -18.53) * mm});
            skLineSegment(sketch, "E566.MirrorCS", {"start": v(112.83, -18.53) * mm, "end": v(112.83, -18.83) * mm});
            skLineSegment(sketch, "E567.MirrorCS", {"start": v(112.63, -25.53) * mm, "end": v(112.33, -25.53) * mm});
            skLineSegment(sketch, "E568.MirrorCS", {"start": v(118.23, -11.93) * mm, "end": v(118.73, -11.93) * mm});
            skArc(sketch, "E569.MirrorCS", {"start": v(112.33, -30.43) * mm, "mid": v(112.77, -31.5) * mm, "end": v(113.83, -31.93) * mm});
            skLineSegment(sketch, "E570.MirrorCS", {"start": v(118.73, -12.23) * mm, "end": v(118.73, -11.93) * mm});
            skArc(sketch, "E571.MirrorCS", {"start": v(117.84, -18.5) * mm, "mid": v(118.28, -19.15) * mm, "end": v(118.43, -19.92) * mm});
            skLineSegment(sketch, "E572.MirrorCS", {"start": v(118.93, -31.43) * mm, "end": v(119.23, -31.43) * mm});
            skLineSegment(sketch, "E573.MirrorCS", {"start": v(119.23, -13.73) * mm, "end": v(119.23, -12.43) * mm});
            skLineSegment(sketch, "E574.MirrorCS", {"start": v(120.32, -18.03) * mm, "end": v(124.34, -18.03) * mm});
            skLineSegment(sketch, "E575.MirrorCS", {"start": v(114.13, -25.03) * mm, "end": v(112.83, -25.03) * mm});
            skLineSegment(sketch, "E576.MirrorCS", {"start": v(114.13, -18.83) * mm, "end": v(112.83, -18.83) * mm});
            skLineSegment(sketch, "E577.MirrorCS", {"start": v(118.93, -12.43) * mm, "end": v(119.23, -12.43) * mm});
            skArc(sketch, "E578.MirrorCS", {"start": v(117.84, -25.35) * mm, "mid": v(118.28, -24.7) * mm, "end": v(118.43, -23.94) * mm});
            skArc(sketch, "E579.MirrorCS", {"start": v(118.73, -31.63) * mm, "mid": v(118.79, -31.49) * mm, "end": v(118.93, -31.43) * mm});
            skArc(sketch, "E580.MirrorCS", {"start": v(118.73, -12.23) * mm, "mid": v(118.79, -12.37) * mm, "end": v(118.93, -12.43) * mm});
            skLineSegment(sketch, "E581.MirrorCS", {"start": v(118.73, -31.63) * mm, "end": v(118.73, -31.93) * mm});
            skLineSegment(sketch, "E582.MirrorCS", {"start": v(120.32, -25.83) * mm, "end": v(124.34, -25.83) * mm});
            skLineSegment(sketch, "E583.MirrorCS", {"start": v(118.23, -31.93) * mm, "end": v(118.73, -31.93) * mm});
            skLineSegment(sketch, "E584.MirrorCS", {"start": v(119.23, -30.13) * mm, "end": v(119.23, -31.43) * mm});
            skArc(sketch, "E585.MirrorCS", {"start": v(120.32, -18.03) * mm, "mid": v(119.55, -17.88) * mm, "end": v(118.9, -17.44) * mm});
            skPoint(sketch, "E586.MirrorP", {"position": v(112.33, -31.93) * mm});
            skLineSegment(sketch, "E587.MirrorCS", {"start": v(113.83, -31.93) * mm, "end": v(118.23, -31.93) * mm});
            skPoint(sketch, "E588.MirrorP", {"position": v(118.43, -25.83) * mm});
            skLineSegment(sketch, "E589.MirrorCS", {"start": v(113.83, -11.93) * mm, "end": v(118.23, -11.93) * mm});
            skArc(sketch, "E590.MirrorCS", {"start": v(120.32, -25.83) * mm, "mid": v(119.55, -25.98) * mm, "end": v(118.9, -26.42) * mm});
            skArc(sketch, "E591.MirrorCS", {"start": v(112.33, -13.43) * mm, "mid": v(112.77, -12.37) * mm, "end": v(113.83, -11.93) * mm});
            skPoint(sketch, "E592.MirrorP", {"position": v(118.43, -24.77) * mm});
            skLineSegment(sketch, "E593.MirrorCS", {"start": v(116.83, -13.73) * mm, "end": v(116.83, -15.37) * mm});
            skLineSegment(sketch, "E594.MirrorCS", {"start": v(118.9, -17.44) * mm, "end": v(116.83, -15.37) * mm});
            skPoint(sketch, "E595.MirrorP", {"position": v(118.43, -19.1) * mm});
            skLineSegment(sketch, "E596.MirrorCS", {"start": v(114.13, -27.43) * mm, "end": v(114.13, -25.03) * mm});
            skLineSegment(sketch, "E597.MirrorCS", {"start": v(117.84, -25.35) * mm, "end": v(115.77, -27.43) * mm});
            skLineSegment(sketch, "E598.MirrorCS", {"start": v(116.83, -30.13) * mm, "end": v(119.23, -30.13) * mm});
            skLineSegment(sketch, "E599.MirrorCS", {"start": v(114.13, -27.43) * mm, "end": v(115.77, -27.43) * mm});
            skLineSegment(sketch, "E600.MirrorCS", {"start": v(112.33, -30.43) * mm, "end": v(112.33, -27.43) * mm});
            skLineSegment(sketch, "E601.MirrorCS", {"start": v(113.83, -11.93) * mm, "end": v(116.83, -11.93) * mm});
            skLineSegment(sketch, "E602.MirrorCS", {"start": v(112.33, -18.33) * mm, "end": v(112.33, -13.43) * mm});
            skLineSegment(sketch, "E603.MirrorCS", {"start": v(116.83, -13.73) * mm, "end": v(119.23, -13.73) * mm});
            skLineSegment(sketch, "E604.MirrorCS", {"start": v(118.9, -26.42) * mm, "end": v(116.83, -28.5) * mm});
            skPoint(sketch, "E605.MirrorP", {"position": v(119.49, -25.83) * mm});
            skLineSegment(sketch, "E606.MirrorCS", {"start": v(114.13, -16.43) * mm, "end": v(114.13, -18.83) * mm});
            skLineSegment(sketch, "E607.MirrorCS", {"start": v(112.33, -13.43) * mm, "end": v(112.33, -16.43) * mm});
            skPoint(sketch, "E608.MirrorP", {"position": v(112.83, -25.53) * mm});
            skPoint(sketch, "E609.MirrorP", {"position": v(112.33, -11.93) * mm});
            skPoint(sketch, "E610.MirrorP", {"position": v(112.83, -18.33) * mm});
            skLineSegment(sketch, "E611.MirrorCS", {"start": v(117.84, -18.5) * mm, "end": v(115.77, -16.43) * mm});
            skLineSegment(sketch, "E612.MirrorCS", {"start": v(114.13, -16.43) * mm, "end": v(115.77, -16.43) * mm});
            skLineSegment(sketch, "E613.MirrorCS", {"start": v(112.33, -30.43) * mm, "end": v(112.33, -25.53) * mm});
            skLineSegment(sketch, "E614.MirrorCS", {"start": v(113.83, -31.93) * mm, "end": v(116.83, -31.93) * mm});
            skPoint(sketch, "E615.MirrorP", {"position": v(118.43, -18.03) * mm});
            skPoint(sketch, "E616.MirrorP", {"position": v(119.49, -18.03) * mm});
            skLineSegment(sketch, "E617.MirrorCS", {"start": v(116.83, -30.13) * mm, "end": v(116.83, -28.5) * mm});
            skSolve(sketch);
        }
        {
            var Q0;
            Q0=makeQuery(id+"F10.imprint","IMPRINT",FACE,{"disambiguationData":[TD([[makeQuery(id+"F10.imprint","IMPRINT",EDGE,{"derivedFrom":sQuery(id+"F10.wireOp",EDGE,"E516.bottom")}),-1.0]])]});
            extrude(context, id + "F11", {"entities" : qUnion([Q0]), "endBound" : BoundingType.SYMMETRIC, "depth" : 221 * mm, "offsetDistance" : 25 * mm});
        }
        {
            var Q0;
            Q0=qCreatedBy(makeId("Top.planeOp"),FACE);
            var sketch = newSketch(context, id + "F12", { "sketchPlane" : qUnion([Q0])});
            skCircle(sketch, "E618", {"center": v(28.94, -55.75) * mm, "radius": 2.5 * mm});
            skLineSegment(sketch, "E619.bottom", {"start": v(37.44, -65.75) * mm, "end": v(33.04, -65.75) * mm});
            skLineSegment(sketch, "E619.top", {"start": v(37.44, -45.75) * mm, "end": v(33.04, -45.75) * mm});
            skLineSegment(sketch, "E619.left", {"start": v(38.94, -64.25) * mm, "end": v(38.94, -59.35) * mm});
            skLineSegment(sketch, "E620.bottom", {"start": v(30.95, -59.65) * mm, "end": v(26.93, -59.65) * mm});
            skLineSegment(sketch, "E620.top", {"start": v(30.95, -51.85) * mm, "end": v(26.93, -51.85) * mm});
            skLineSegment(sketch, "E620.left", {"start": v(32.84, -57.76) * mm, "end": v(32.84, -53.74) * mm});
            skLineSegment(sketch, "E620.right", {"start": v(25.04, -57.76) * mm, "end": v(25.04, -53.74) * mm});
            skLineSegment(sketch, "E621.bottom", {"start": v(37.44, -45.75) * mm, "end": v(34.44, -45.75) * mm});
            skLineSegment(sketch, "E621.left", {"start": v(38.94, -47.25) * mm, "end": v(38.94, -50.25) * mm});
            skLineSegment(sketch, "E621.right", {"start": v(34.44, -47.55) * mm, "end": v(34.44, -49.2) * mm});
            skLineSegment(sketch, "E622", {"start": v(33.43, -52.33) * mm, "end": v(35.5, -50.25) * mm});
            skLineSegment(sketch, "E623.MirrorCS", {"start": v(32.37, -51.27) * mm, "end": v(34.44, -49.2) * mm});
            skLineSegment(sketch, "E624", {"start": v(37.14, -50.25) * mm, "end": v(37.14, -52.65) * mm});
            skLineSegment(sketch, "E625", {"start": v(38.64, -52.15) * mm, "end": v(38.94, -52.15) * mm});
            skLineSegment(sketch, "E626", {"start": v(37.14, -52.65) * mm, "end": v(38.44, -52.65) * mm});
            skLineSegment(sketch, "E627", {"start": v(38.44, -52.35) * mm, "end": v(38.44, -52.65) * mm});
            skPoint(sketch, "E628.visualSharp", {"position": v(38.44, -52.15) * mm});
            skArc(sketch, "E628.filletArc", {"start": v(38.64, -52.15) * mm, "mid": v(38.5, -52.21) * mm, "end": v(38.44, -52.35) * mm});
            skPoint(sketch, "E629.newPointA", {"position": v(32.84, -52.91) * mm});
            skArc(sketch, "E629.filletArc", {"start": v(33.43, -52.33) * mm, "mid": v(33, -52.98) * mm, "end": v(32.84, -53.74) * mm});
            skPoint(sketch, "E630.newPointA", {"position": v(31.78, -51.85) * mm});
            skPoint(sketch, "E630.newPointB", {"position": v(32.84, -51.85) * mm});
            skArc(sketch, "E630.filletArc", {"start": v(30.95, -51.85) * mm, "mid": v(31.72, -51.7) * mm, "end": v(32.37, -51.27) * mm});
            skLineSegment(sketch, "E631.MirrorCS", {"start": v(34.44, -47.55) * mm, "end": v(32.04, -47.55) * mm});
            skLineSegment(sketch, "E632.MirrorCS", {"start": v(32.04, -47.55) * mm, "end": v(32.04, -46.25) * mm});
            skPoint(sketch, "E633.visualSharp", {"position": v(38.94, -45.75) * mm});
            skArc(sketch, "E633.filletArc", {"start": v(38.94, -47.25) * mm, "mid": v(38.5, -46.2) * mm, "end": v(37.44, -45.75) * mm});
            skLineSegment(sketch, "E634.trimOffspring", {"start": v(37.14, -50.25) * mm, "end": v(35.5, -50.25) * mm});
            skLineSegment(sketch, "E635.MirrorCS", {"start": v(38.64, -59.35) * mm, "end": v(38.94, -59.35) * mm});
            skArc(sketch, "E636.MirrorCS", {"start": v(38.64, -59.35) * mm, "mid": v(38.5, -59.3) * mm, "end": v(38.44, -59.15) * mm});
            skLineSegment(sketch, "E637.MirrorCS", {"start": v(38.44, -59.15) * mm, "end": v(38.44, -58.85) * mm});
            skArc(sketch, "E638.MirrorCS", {"start": v(33.43, -59.18) * mm, "mid": v(33, -58.53) * mm, "end": v(32.84, -57.76) * mm});
            skLineSegment(sketch, "E639.MirrorCS", {"start": v(37.14, -61.25) * mm, "end": v(35.5, -61.25) * mm});
            skLineSegment(sketch, "E640.MirrorCS", {"start": v(37.14, -58.85) * mm, "end": v(38.44, -58.85) * mm});
            skLineSegment(sketch, "E641.MirrorCS", {"start": v(37.44, -65.75) * mm, "end": v(34.44, -65.75) * mm});
            skPoint(sketch, "E642.MirrorP", {"position": v(38.44, -59.35) * mm});
            skLineSegment(sketch, "E643.MirrorCS", {"start": v(32.04, -63.95) * mm, "end": v(32.04, -65.25) * mm});
            skLineSegment(sketch, "E644.MirrorCS", {"start": v(34.44, -63.95) * mm, "end": v(32.04, -63.95) * mm});
            skLineSegment(sketch, "E645.MirrorCS", {"start": v(37.14, -61.25) * mm, "end": v(37.14, -58.85) * mm});
            skLineSegment(sketch, "E646.MirrorCS", {"start": v(38.94, -64.25) * mm, "end": v(38.94, -61.25) * mm});
            skLineSegment(sketch, "E647.MirrorCS", {"start": v(33.43, -59.18) * mm, "end": v(35.5, -61.25) * mm});
            skPoint(sketch, "E648.MirrorP", {"position": v(32.84, -58.6) * mm});
            skPoint(sketch, "E649.MirrorP", {"position": v(38.94, -65.75) * mm});
            skPoint(sketch, "E650.MirrorP", {"position": v(32.84, -59.65) * mm});
            skLineSegment(sketch, "E651.MirrorCS", {"start": v(32.37, -60.24) * mm, "end": v(34.44, -62.31) * mm});
            skPoint(sketch, "E652.MirrorP", {"position": v(31.78, -59.65) * mm});
            skArc(sketch, "E653.MirrorCS", {"start": v(38.94, -64.25) * mm, "mid": v(38.5, -65.31) * mm, "end": v(37.44, -65.75) * mm});
            skLineSegment(sketch, "E654.MirrorCS", {"start": v(34.44, -63.95) * mm, "end": v(34.44, -62.31) * mm});
            skArc(sketch, "E655.MirrorCS", {"start": v(30.95, -59.65) * mm, "mid": v(31.72, -59.8) * mm, "end": v(32.37, -60.24) * mm});
            skLineSegment(sketch, "E656.trimOffspring", {"start": v(38.94, -52.15) * mm, "end": v(38.94, -47.25) * mm});
            skLineSegment(sketch, "E657.MirrorCS", {"start": v(32.54, -46.05) * mm, "end": v(32.54, -45.75) * mm});
            skArc(sketch, "E658.MirrorCS", {"start": v(32.54, -46.05) * mm, "mid": v(32.48, -46.2) * mm, "end": v(32.34, -46.25) * mm});
            skLineSegment(sketch, "E659.MirrorCS", {"start": v(32.34, -46.25) * mm, "end": v(32.04, -46.25) * mm});
            skLineSegment(sketch, "E660", {"start": v(33.04, -45.75) * mm, "end": v(32.54, -45.75) * mm});
            skLineSegment(sketch, "E661.MirrorCS", {"start": v(32.54, -65.45) * mm, "end": v(32.54, -65.75) * mm});
            skLineSegment(sketch, "E662.MirrorCS", {"start": v(32.34, -65.25) * mm, "end": v(32.04, -65.25) * mm});
            skLineSegment(sketch, "E663.MirrorCS", {"start": v(33.04, -65.75) * mm, "end": v(32.54, -65.75) * mm});
            skArc(sketch, "E664.MirrorCS", {"start": v(32.54, -65.45) * mm, "mid": v(32.48, -65.31) * mm, "end": v(32.34, -65.25) * mm});
            skArc(sketch, "E665.MirrorCS", {"start": v(19.24, -59.35) * mm, "mid": v(19.38, -59.3) * mm, "end": v(19.44, -59.15) * mm});
            skLineSegment(sketch, "E666.MirrorCS", {"start": v(19.24, -52.15) * mm, "end": v(18.94, -52.15) * mm});
            skLineSegment(sketch, "E667.MirrorCS", {"start": v(19.44, -59.15) * mm, "end": v(19.44, -58.85) * mm});
            skArc(sketch, "E668.MirrorCS", {"start": v(19.24, -52.15) * mm, "mid": v(19.38, -52.21) * mm, "end": v(19.44, -52.35) * mm});
            skLineSegment(sketch, "E669.MirrorCS", {"start": v(19.44, -52.35) * mm, "end": v(19.44, -52.65) * mm});
            skLineSegment(sketch, "E670.MirrorCS", {"start": v(19.24, -59.35) * mm, "end": v(18.94, -59.35) * mm});
            skLineSegment(sketch, "E671.MirrorCS", {"start": v(24.84, -45.75) * mm, "end": v(25.34, -45.75) * mm});
            skArc(sketch, "E672.MirrorCS", {"start": v(18.94, -64.25) * mm, "mid": v(19.38, -65.31) * mm, "end": v(20.44, -65.75) * mm});
            skLineSegment(sketch, "E673.MirrorCS", {"start": v(25.34, -46.05) * mm, "end": v(25.34, -45.75) * mm});
            skArc(sketch, "E674.MirrorCS", {"start": v(24.45, -52.33) * mm, "mid": v(24.89, -52.98) * mm, "end": v(25.04, -53.74) * mm});
            skLineSegment(sketch, "E675.MirrorCS", {"start": v(25.54, -65.25) * mm, "end": v(25.84, -65.25) * mm});
            skLineSegment(sketch, "E676.MirrorCS", {"start": v(25.84, -47.55) * mm, "end": v(25.84, -46.25) * mm});
            skLineSegment(sketch, "E677.MirrorCS", {"start": v(26.93, -51.85) * mm, "end": v(30.95, -51.85) * mm});
            skLineSegment(sketch, "E678.MirrorCS", {"start": v(20.74, -58.85) * mm, "end": v(19.44, -58.85) * mm});
            skLineSegment(sketch, "E679.MirrorCS", {"start": v(20.74, -52.65) * mm, "end": v(19.44, -52.65) * mm});
            skLineSegment(sketch, "E680.MirrorCS", {"start": v(25.54, -46.25) * mm, "end": v(25.84, -46.25) * mm});
            skArc(sketch, "E681.MirrorCS", {"start": v(24.45, -59.18) * mm, "mid": v(24.89, -58.53) * mm, "end": v(25.04, -57.76) * mm});
            skArc(sketch, "E682.MirrorCS", {"start": v(25.34, -65.45) * mm, "mid": v(25.4, -65.31) * mm, "end": v(25.54, -65.25) * mm});
            skArc(sketch, "E683.MirrorCS", {"start": v(25.34, -46.05) * mm, "mid": v(25.4, -46.2) * mm, "end": v(25.54, -46.25) * mm});
            skLineSegment(sketch, "E684.MirrorCS", {"start": v(25.34, -65.45) * mm, "end": v(25.34, -65.75) * mm});
            skLineSegment(sketch, "E685.MirrorCS", {"start": v(26.93, -59.65) * mm, "end": v(30.95, -59.65) * mm});
            skLineSegment(sketch, "E686.MirrorCS", {"start": v(24.84, -65.75) * mm, "end": v(25.34, -65.75) * mm});
            skLineSegment(sketch, "E687.MirrorCS", {"start": v(25.84, -63.95) * mm, "end": v(25.84, -65.25) * mm});
            skArc(sketch, "E688.MirrorCS", {"start": v(26.93, -51.85) * mm, "mid": v(26.16, -51.7) * mm, "end": v(25.52, -51.27) * mm});
            skPoint(sketch, "E689.MirrorP", {"position": v(18.94, -65.75) * mm});
            skLineSegment(sketch, "E690.MirrorCS", {"start": v(20.44, -65.75) * mm, "end": v(24.84, -65.75) * mm});
            skPoint(sketch, "E691.MirrorP", {"position": v(25.04, -59.65) * mm});
            skLineSegment(sketch, "E692.MirrorCS", {"start": v(20.44, -45.75) * mm, "end": v(24.84, -45.75) * mm});
            skArc(sketch, "E693.MirrorCS", {"start": v(26.93, -59.65) * mm, "mid": v(26.16, -59.8) * mm, "end": v(25.52, -60.24) * mm});
            skArc(sketch, "E694.MirrorCS", {"start": v(18.94, -47.25) * mm, "mid": v(19.38, -46.2) * mm, "end": v(20.44, -45.75) * mm});
            skPoint(sketch, "E695.MirrorP", {"position": v(25.04, -58.6) * mm});
            skLineSegment(sketch, "E696.MirrorCS", {"start": v(23.44, -47.55) * mm, "end": v(23.44, -49.2) * mm});
            skLineSegment(sketch, "E697.MirrorCS", {"start": v(25.52, -51.27) * mm, "end": v(23.44, -49.2) * mm});
            skPoint(sketch, "E698.MirrorP", {"position": v(25.04, -52.91) * mm});
            skLineSegment(sketch, "E699.MirrorCS", {"start": v(20.74, -61.25) * mm, "end": v(20.74, -58.85) * mm});
            skLineSegment(sketch, "E700.MirrorCS", {"start": v(24.45, -59.18) * mm, "end": v(22.38, -61.25) * mm});
            skLineSegment(sketch, "E701.MirrorCS", {"start": v(23.44, -63.95) * mm, "end": v(25.84, -63.95) * mm});
            skLineSegment(sketch, "E702.MirrorCS", {"start": v(20.74, -61.25) * mm, "end": v(22.38, -61.25) * mm});
            skLineSegment(sketch, "E703.MirrorCS", {"start": v(18.94, -64.25) * mm, "end": v(18.94, -61.25) * mm});
            skLineSegment(sketch, "E704.MirrorCS", {"start": v(20.44, -45.75) * mm, "end": v(23.44, -45.75) * mm});
            skLineSegment(sketch, "E705.MirrorCS", {"start": v(18.94, -52.15) * mm, "end": v(18.94, -47.25) * mm});
            skLineSegment(sketch, "E706.MirrorCS", {"start": v(23.44, -47.55) * mm, "end": v(25.84, -47.55) * mm});
            skLineSegment(sketch, "E707.MirrorCS", {"start": v(25.52, -60.24) * mm, "end": v(23.44, -62.31) * mm});
            skPoint(sketch, "E708.MirrorP", {"position": v(26.1, -59.65) * mm});
            skLineSegment(sketch, "E709.MirrorCS", {"start": v(20.74, -50.25) * mm, "end": v(20.74, -52.65) * mm});
            skLineSegment(sketch, "E710.MirrorCS", {"start": v(18.94, -47.25) * mm, "end": v(18.94, -50.25) * mm});
            skPoint(sketch, "E711.MirrorP", {"position": v(19.44, -59.35) * mm});
            skPoint(sketch, "E712.MirrorP", {"position": v(18.94, -45.75) * mm});
            skPoint(sketch, "E713.MirrorP", {"position": v(19.44, -52.15) * mm});
            skLineSegment(sketch, "E714.MirrorCS", {"start": v(24.45, -52.33) * mm, "end": v(22.38, -50.25) * mm});
            skLineSegment(sketch, "E715.MirrorCS", {"start": v(20.74, -50.25) * mm, "end": v(22.38, -50.25) * mm});
            skLineSegment(sketch, "E716.MirrorCS", {"start": v(18.94, -64.25) * mm, "end": v(18.94, -59.35) * mm});
            skLineSegment(sketch, "E717.MirrorCS", {"start": v(20.44, -65.75) * mm, "end": v(23.44, -65.75) * mm});
            skPoint(sketch, "E718.MirrorP", {"position": v(25.04, -51.85) * mm});
            skPoint(sketch, "E719.MirrorP", {"position": v(26.1, -51.85) * mm});
            skLineSegment(sketch, "E720.MirrorCS", {"start": v(23.44, -63.95) * mm, "end": v(23.44, -62.31) * mm});
            skSolve(sketch);
        }
        {
            var Q0;
            Q0=makeQuery(id+"F12.imprint","IMPRINT",FACE,{"disambiguationData":[TD([[makeQuery(id+"F12.imprint","IMPRINT",EDGE,{"derivedFrom":sQuery(id+"F12.wireOp",EDGE,"E619.bottom")}),-1.0]])]});
            extrude(context, id + "F13", {"entities" : qUnion([Q0]), "endBound" : BoundingType.SYMMETRIC, "depth" : 203 * mm, "offsetDistance" : 25 * mm});
        }
        {
            var Q0;
            Q0=qCreatedBy(makeId("Top.planeOp"),FACE);
            var sketch = newSketch(context, id + "F14", { "sketchPlane" : qUnion([Q0])});
            skCircle(sketch, "E721", {"center": v(71.03, 71.04) * mm, "radius": 2.5 * mm});
            skLineSegment(sketch, "E722.bottom", {"start": v(79.53, 61.04) * mm, "end": v(75.13, 61.04) * mm});
            skLineSegment(sketch, "E722.top", {"start": v(79.53, 81.04) * mm, "end": v(75.13, 81.04) * mm});
            skLineSegment(sketch, "E722.left", {"start": v(81.03, 62.54) * mm, "end": v(81.03, 67.44) * mm});
            skLineSegment(sketch, "E723.bottom", {"start": v(73.05, 67.14) * mm, "end": v(69.02, 67.14) * mm});
            skLineSegment(sketch, "E723.top", {"start": v(73.05, 74.94) * mm, "end": v(69.02, 74.94) * mm});
            skLineSegment(sketch, "E723.left", {"start": v(74.93, 69.03) * mm, "end": v(74.93, 73.06) * mm});
            skLineSegment(sketch, "E723.right", {"start": v(67.13, 69.03) * mm, "end": v(67.13, 73.06) * mm});
            skLineSegment(sketch, "E724.bottom", {"start": v(79.53, 81.04) * mm, "end": v(76.53, 81.04) * mm});
            skLineSegment(sketch, "E724.left", {"start": v(81.03, 79.54) * mm, "end": v(81.03, 76.54) * mm});
            skLineSegment(sketch, "E724.right", {"start": v(76.53, 79.24) * mm, "end": v(76.53, 77.6) * mm});
            skLineSegment(sketch, "E725", {"start": v(75.52, 74.47) * mm, "end": v(77.6, 76.54) * mm});
            skLineSegment(sketch, "E726.MirrorCS", {"start": v(74.46, 75.53) * mm, "end": v(76.53, 77.6) * mm});
            skLineSegment(sketch, "E727", {"start": v(79.23, 76.54) * mm, "end": v(79.23, 74.14) * mm});
            skLineSegment(sketch, "E728", {"start": v(80.73, 74.64) * mm, "end": v(81.03, 74.64) * mm});
            skLineSegment(sketch, "E729", {"start": v(79.23, 74.14) * mm, "end": v(80.53, 74.14) * mm});
            skLineSegment(sketch, "E730", {"start": v(80.53, 74.44) * mm, "end": v(80.53, 74.14) * mm});
            skPoint(sketch, "E731.visualSharp", {"position": v(80.53, 74.64) * mm});
            skArc(sketch, "E731.filletArc", {"start": v(80.73, 74.64) * mm, "mid": v(80.6, 74.59) * mm, "end": v(80.53, 74.44) * mm});
            skPoint(sketch, "E732.newPointA", {"position": v(74.93, 73.88) * mm});
            skArc(sketch, "E732.filletArc", {"start": v(75.52, 74.47) * mm, "mid": v(75.09, 73.82) * mm, "end": v(74.93, 73.06) * mm});
            skPoint(sketch, "E733.newPointA", {"position": v(73.87, 74.94) * mm});
            skPoint(sketch, "E733.newPointB", {"position": v(74.93, 74.94) * mm});
            skArc(sketch, "E733.filletArc", {"start": v(73.05, 74.94) * mm, "mid": v(73.81, 75.1) * mm, "end": v(74.46, 75.53) * mm});
            skLineSegment(sketch, "E734.MirrorCS", {"start": v(76.53, 79.24) * mm, "end": v(74.13, 79.24) * mm});
            skLineSegment(sketch, "E735.MirrorCS", {"start": v(74.13, 79.24) * mm, "end": v(74.13, 80.54) * mm});
            skPoint(sketch, "E736.visualSharp", {"position": v(81.03, 81.04) * mm});
            skArc(sketch, "E736.filletArc", {"start": v(81.03, 79.54) * mm, "mid": v(80.6, 80.6) * mm, "end": v(79.53, 81.04) * mm});
            skLineSegment(sketch, "E737.trimOffspring", {"start": v(79.23, 76.54) * mm, "end": v(77.6, 76.54) * mm});
            skLineSegment(sketch, "E738.MirrorCS", {"start": v(80.73, 67.44) * mm, "end": v(81.03, 67.44) * mm});
            skArc(sketch, "E739.MirrorCS", {"start": v(80.73, 67.44) * mm, "mid": v(80.6, 67.5) * mm, "end": v(80.53, 67.64) * mm});
            skLineSegment(sketch, "E740.MirrorCS", {"start": v(80.53, 67.64) * mm, "end": v(80.53, 67.94) * mm});
            skArc(sketch, "E741.MirrorCS", {"start": v(75.52, 67.62) * mm, "mid": v(75.09, 68.27) * mm, "end": v(74.93, 69.03) * mm});
            skLineSegment(sketch, "E742.MirrorCS", {"start": v(79.23, 65.54) * mm, "end": v(77.6, 65.54) * mm});
            skLineSegment(sketch, "E743.MirrorCS", {"start": v(79.23, 67.94) * mm, "end": v(80.53, 67.94) * mm});
            skLineSegment(sketch, "E744.MirrorCS", {"start": v(79.53, 61.04) * mm, "end": v(76.53, 61.04) * mm});
            skPoint(sketch, "E745.MirrorP", {"position": v(80.53, 67.44) * mm});
            skLineSegment(sketch, "E746.MirrorCS", {"start": v(74.13, 62.84) * mm, "end": v(74.13, 61.54) * mm});
            skLineSegment(sketch, "E747.MirrorCS", {"start": v(76.53, 62.84) * mm, "end": v(74.13, 62.84) * mm});
            skLineSegment(sketch, "E748.MirrorCS", {"start": v(79.23, 65.54) * mm, "end": v(79.23, 67.94) * mm});
            skLineSegment(sketch, "E749.MirrorCS", {"start": v(81.03, 62.54) * mm, "end": v(81.03, 65.54) * mm});
            skLineSegment(sketch, "E750.MirrorCS", {"start": v(75.52, 67.62) * mm, "end": v(77.6, 65.54) * mm});
            skPoint(sketch, "E751.MirrorP", {"position": v(74.93, 68.2) * mm});
            skPoint(sketch, "E752.MirrorP", {"position": v(81.03, 61.04) * mm});
            skPoint(sketch, "E753.MirrorP", {"position": v(74.93, 67.14) * mm});
            skLineSegment(sketch, "E754.MirrorCS", {"start": v(74.46, 66.56) * mm, "end": v(76.53, 64.48) * mm});
            skPoint(sketch, "E755.MirrorP", {"position": v(73.87, 67.14) * mm});
            skArc(sketch, "E756.MirrorCS", {"start": v(81.03, 62.54) * mm, "mid": v(80.6, 61.48) * mm, "end": v(79.53, 61.04) * mm});
            skLineSegment(sketch, "E757.MirrorCS", {"start": v(76.53, 62.84) * mm, "end": v(76.53, 64.48) * mm});
            skArc(sketch, "E758.MirrorCS", {"start": v(73.05, 67.14) * mm, "mid": v(73.81, 67) * mm, "end": v(74.46, 66.56) * mm});
            skLineSegment(sketch, "E759.trimOffspring", {"start": v(81.03, 74.64) * mm, "end": v(81.03, 79.54) * mm});
            skLineSegment(sketch, "E760.MirrorCS", {"start": v(74.63, 80.74) * mm, "end": v(74.63, 81.04) * mm});
            skArc(sketch, "E761.MirrorCS", {"start": v(74.63, 80.74) * mm, "mid": v(74.58, 80.6) * mm, "end": v(74.43, 80.54) * mm});
            skLineSegment(sketch, "E762.MirrorCS", {"start": v(74.43, 80.54) * mm, "end": v(74.13, 80.54) * mm});
            skLineSegment(sketch, "E763", {"start": v(75.13, 81.04) * mm, "end": v(74.63, 81.04) * mm});
            skLineSegment(sketch, "E764.MirrorCS", {"start": v(74.63, 61.34) * mm, "end": v(74.63, 61.04) * mm});
            skLineSegment(sketch, "E765.MirrorCS", {"start": v(74.43, 61.54) * mm, "end": v(74.13, 61.54) * mm});
            skLineSegment(sketch, "E766.MirrorCS", {"start": v(75.13, 61.04) * mm, "end": v(74.63, 61.04) * mm});
            skArc(sketch, "E767.MirrorCS", {"start": v(74.63, 61.34) * mm, "mid": v(74.58, 61.49) * mm, "end": v(74.43, 61.54) * mm});
            skArc(sketch, "E768.MirrorCS", {"start": v(61.33, 67.44) * mm, "mid": v(61.48, 67.5) * mm, "end": v(61.53, 67.64) * mm});
            skLineSegment(sketch, "E769.MirrorCS", {"start": v(61.33, 74.64) * mm, "end": v(61.03, 74.64) * mm});
            skLineSegment(sketch, "E770.MirrorCS", {"start": v(61.53, 67.64) * mm, "end": v(61.53, 67.94) * mm});
            skArc(sketch, "E771.MirrorCS", {"start": v(61.33, 74.64) * mm, "mid": v(61.48, 74.59) * mm, "end": v(61.53, 74.44) * mm});
            skLineSegment(sketch, "E772.MirrorCS", {"start": v(61.53, 74.44) * mm, "end": v(61.53, 74.14) * mm});
            skLineSegment(sketch, "E773.MirrorCS", {"start": v(61.33, 67.44) * mm, "end": v(61.03, 67.44) * mm});
            skLineSegment(sketch, "E774.MirrorCS", {"start": v(66.93, 81.04) * mm, "end": v(67.43, 81.04) * mm});
            skArc(sketch, "E775.MirrorCS", {"start": v(61.03, 62.54) * mm, "mid": v(61.47, 61.48) * mm, "end": v(62.53, 61.04) * mm});
            skLineSegment(sketch, "E776.MirrorCS", {"start": v(67.43, 80.74) * mm, "end": v(67.43, 81.04) * mm});
            skArc(sketch, "E777.MirrorCS", {"start": v(66.55, 74.47) * mm, "mid": v(66.98, 73.82) * mm, "end": v(67.13, 73.06) * mm});
            skLineSegment(sketch, "E778.MirrorCS", {"start": v(67.63, 61.54) * mm, "end": v(67.93, 61.54) * mm});
            skLineSegment(sketch, "E779.MirrorCS", {"start": v(67.93, 79.24) * mm, "end": v(67.93, 80.54) * mm});
            skLineSegment(sketch, "E780.MirrorCS", {"start": v(69.02, 74.94) * mm, "end": v(73.05, 74.94) * mm});
            skLineSegment(sketch, "E781.MirrorCS", {"start": v(62.83, 67.94) * mm, "end": v(61.53, 67.94) * mm});
            skLineSegment(sketch, "E782.MirrorCS", {"start": v(62.83, 74.14) * mm, "end": v(61.53, 74.14) * mm});
            skLineSegment(sketch, "E783.MirrorCS", {"start": v(67.63, 80.54) * mm, "end": v(67.93, 80.54) * mm});
            skArc(sketch, "E784.MirrorCS", {"start": v(66.55, 67.62) * mm, "mid": v(66.98, 68.27) * mm, "end": v(67.13, 69.03) * mm});
            skArc(sketch, "E785.MirrorCS", {"start": v(67.43, 61.34) * mm, "mid": v(67.5, 61.49) * mm, "end": v(67.63, 61.54) * mm});
            skArc(sketch, "E786.MirrorCS", {"start": v(67.43, 80.74) * mm, "mid": v(67.5, 80.6) * mm, "end": v(67.63, 80.54) * mm});
            skLineSegment(sketch, "E787.MirrorCS", {"start": v(67.43, 61.34) * mm, "end": v(67.43, 61.04) * mm});
            skLineSegment(sketch, "E788.MirrorCS", {"start": v(69.02, 67.14) * mm, "end": v(73.05, 67.14) * mm});
            skLineSegment(sketch, "E789.MirrorCS", {"start": v(66.93, 61.04) * mm, "end": v(67.43, 61.04) * mm});
            skLineSegment(sketch, "E790.MirrorCS", {"start": v(67.93, 62.84) * mm, "end": v(67.93, 61.54) * mm});
            skArc(sketch, "E791.MirrorCS", {"start": v(69.02, 74.94) * mm, "mid": v(68.26, 75.1) * mm, "end": v(67.6, 75.53) * mm});
            skPoint(sketch, "E792.MirrorP", {"position": v(61.03, 61.04) * mm});
            skLineSegment(sketch, "E793.MirrorCS", {"start": v(62.53, 61.04) * mm, "end": v(66.93, 61.04) * mm});
            skPoint(sketch, "E794.MirrorP", {"position": v(67.13, 67.14) * mm});
            skLineSegment(sketch, "E795.MirrorCS", {"start": v(62.53, 81.04) * mm, "end": v(66.93, 81.04) * mm});
            skArc(sketch, "E796.MirrorCS", {"start": v(69.02, 67.14) * mm, "mid": v(68.26, 67) * mm, "end": v(67.6, 66.56) * mm});
            skArc(sketch, "E797.MirrorCS", {"start": v(61.03, 79.54) * mm, "mid": v(61.47, 80.6) * mm, "end": v(62.53, 81.04) * mm});
            skPoint(sketch, "E798.MirrorP", {"position": v(67.13, 68.2) * mm});
            skLineSegment(sketch, "E799.MirrorCS", {"start": v(65.53, 79.24) * mm, "end": v(65.53, 77.6) * mm});
            skLineSegment(sketch, "E800.MirrorCS", {"start": v(67.6, 75.53) * mm, "end": v(65.53, 77.6) * mm});
            skPoint(sketch, "E801.MirrorP", {"position": v(67.13, 73.88) * mm});
            skLineSegment(sketch, "E802.MirrorCS", {"start": v(62.83, 65.54) * mm, "end": v(62.83, 67.94) * mm});
            skLineSegment(sketch, "E803.MirrorCS", {"start": v(66.55, 67.62) * mm, "end": v(64.47, 65.54) * mm});
            skLineSegment(sketch, "E804.MirrorCS", {"start": v(65.53, 62.84) * mm, "end": v(67.93, 62.84) * mm});
            skLineSegment(sketch, "E805.MirrorCS", {"start": v(62.83, 65.54) * mm, "end": v(64.47, 65.54) * mm});
            skLineSegment(sketch, "E806.MirrorCS", {"start": v(61.03, 62.54) * mm, "end": v(61.03, 65.54) * mm});
            skLineSegment(sketch, "E807.MirrorCS", {"start": v(62.53, 81.04) * mm, "end": v(65.53, 81.04) * mm});
            skLineSegment(sketch, "E808.MirrorCS", {"start": v(61.03, 74.64) * mm, "end": v(61.03, 79.54) * mm});
            skLineSegment(sketch, "E809.MirrorCS", {"start": v(65.53, 79.24) * mm, "end": v(67.93, 79.24) * mm});
            skLineSegment(sketch, "E810.MirrorCS", {"start": v(67.6, 66.56) * mm, "end": v(65.53, 64.48) * mm});
            skPoint(sketch, "E811.MirrorP", {"position": v(68.2, 67.14) * mm});
            skLineSegment(sketch, "E812.MirrorCS", {"start": v(62.83, 76.54) * mm, "end": v(62.83, 74.14) * mm});
            skLineSegment(sketch, "E813.MirrorCS", {"start": v(61.03, 79.54) * mm, "end": v(61.03, 76.54) * mm});
            skPoint(sketch, "E814.MirrorP", {"position": v(61.53, 67.44) * mm});
            skPoint(sketch, "E815.MirrorP", {"position": v(61.03, 81.04) * mm});
            skPoint(sketch, "E816.MirrorP", {"position": v(61.53, 74.64) * mm});
            skLineSegment(sketch, "E817.MirrorCS", {"start": v(66.55, 74.47) * mm, "end": v(64.47, 76.54) * mm});
            skLineSegment(sketch, "E818.MirrorCS", {"start": v(62.83, 76.54) * mm, "end": v(64.47, 76.54) * mm});
            skLineSegment(sketch, "E819.MirrorCS", {"start": v(61.03, 62.54) * mm, "end": v(61.03, 67.44) * mm});
            skLineSegment(sketch, "E820.MirrorCS", {"start": v(62.53, 61.04) * mm, "end": v(65.53, 61.04) * mm});
            skPoint(sketch, "E821.MirrorP", {"position": v(67.13, 74.94) * mm});
            skPoint(sketch, "E822.MirrorP", {"position": v(68.2, 74.94) * mm});
            skLineSegment(sketch, "E823.MirrorCS", {"start": v(65.53, 62.84) * mm, "end": v(65.53, 64.48) * mm});
            skSolve(sketch);
        }
        {
            var Q0;
            Q0=makeQuery(id+"F14.imprint","IMPRINT",FACE,{"disambiguationData":[TD([[makeQuery(id+"F14.imprint","IMPRINT",EDGE,{"derivedFrom":sQuery(id+"F14.wireOp",EDGE,"E722.bottom")}),-1.0]])]});
            extrude(context, id + "F15", {"entities" : qUnion([Q0]), "endBound" : BoundingType.SYMMETRIC, "depth" : 195 * mm, "offsetDistance" : 25 * mm});
        }
        {
            var Q0;
            Q0=qCreatedBy(makeId("Top.planeOp"),FACE);
            var sketch = newSketch(context, id + "F16", { "sketchPlane" : qUnion([Q0])});
            skCircle(sketch, "E824", {"center": v(-160.4, -45.54) * mm, "radius": 2.5 * mm});
            skLineSegment(sketch, "E825.bottom", {"start": v(-151.9, -55.54) * mm, "end": v(-156.3, -55.54) * mm});
            skLineSegment(sketch, "E825.top", {"start": v(-151.9, -35.54) * mm, "end": v(-156.3, -35.54) * mm});
            skLineSegment(sketch, "E825.left", {"start": v(-150.4, -54.04) * mm, "end": v(-150.4, -49.14) * mm});
            skLineSegment(sketch, "E826.bottom", {"start": v(-158.38, -49.44) * mm, "end": v(-162.4, -49.44) * mm});
            skLineSegment(sketch, "E826.top", {"start": v(-158.38, -41.64) * mm, "end": v(-162.4, -41.64) * mm});
            skLineSegment(sketch, "E826.left", {"start": v(-156.5, -47.55) * mm, "end": v(-156.5, -43.52) * mm});
            skLineSegment(sketch, "E826.right", {"start": v(-164.3, -47.55) * mm, "end": v(-164.3, -43.52) * mm});
            skLineSegment(sketch, "E827.bottom", {"start": v(-151.9, -35.54) * mm, "end": v(-154.9, -35.54) * mm});
            skLineSegment(sketch, "E827.left", {"start": v(-150.4, -37.04) * mm, "end": v(-150.4, -40.04) * mm});
            skLineSegment(sketch, "E827.right", {"start": v(-154.9, -37.34) * mm, "end": v(-154.9, -38.98) * mm});
            skLineSegment(sketch, "E828", {"start": v(-155.9, -42.11) * mm, "end": v(-153.83, -40.04) * mm});
            skLineSegment(sketch, "E829.MirrorCS", {"start": v(-156.97, -41.05) * mm, "end": v(-154.9, -38.98) * mm});
            skLineSegment(sketch, "E830", {"start": v(-152.2, -40.04) * mm, "end": v(-152.2, -42.44) * mm});
            skLineSegment(sketch, "E831", {"start": v(-150.7, -41.94) * mm, "end": v(-150.4, -41.94) * mm});
            skLineSegment(sketch, "E832", {"start": v(-152.2, -42.44) * mm, "end": v(-150.9, -42.44) * mm});
            skLineSegment(sketch, "E833", {"start": v(-150.9, -42.14) * mm, "end": v(-150.9, -42.44) * mm});
            skPoint(sketch, "E834.visualSharp", {"position": v(-150.9, -41.94) * mm});
            skArc(sketch, "E834.filletArc", {"start": v(-150.7, -41.94) * mm, "mid": v(-150.84, -42) * mm, "end": v(-150.9, -42.14) * mm});
            skPoint(sketch, "E835.newPointA", {"position": v(-156.5, -42.7) * mm});
            skArc(sketch, "E835.filletArc", {"start": v(-155.9, -42.11) * mm, "mid": v(-156.34, -42.76) * mm, "end": v(-156.5, -43.52) * mm});
            skPoint(sketch, "E836.newPointA", {"position": v(-157.56, -41.64) * mm});
            skPoint(sketch, "E836.newPointB", {"position": v(-156.5, -41.64) * mm});
            skArc(sketch, "E836.filletArc", {"start": v(-158.38, -41.64) * mm, "mid": v(-157.62, -41.48) * mm, "end": v(-156.97, -41.05) * mm});
            skLineSegment(sketch, "E837.MirrorCS", {"start": v(-154.9, -37.34) * mm, "end": v(-157.3, -37.34) * mm});
            skLineSegment(sketch, "E838.MirrorCS", {"start": v(-157.3, -37.34) * mm, "end": v(-157.3, -36.04) * mm});
            skPoint(sketch, "E839.visualSharp", {"position": v(-150.4, -35.54) * mm});
            skArc(sketch, "E839.filletArc", {"start": v(-150.4, -37.04) * mm, "mid": v(-150.83, -35.98) * mm, "end": v(-151.9, -35.54) * mm});
            skLineSegment(sketch, "E840.trimOffspring", {"start": v(-152.2, -40.04) * mm, "end": v(-153.83, -40.04) * mm});
            skLineSegment(sketch, "E841.MirrorCS", {"start": v(-150.7, -49.14) * mm, "end": v(-150.4, -49.14) * mm});
            skArc(sketch, "E842.MirrorCS", {"start": v(-150.7, -49.14) * mm, "mid": v(-150.84, -49.08) * mm, "end": v(-150.9, -48.94) * mm});
            skLineSegment(sketch, "E843.MirrorCS", {"start": v(-150.9, -48.94) * mm, "end": v(-150.9, -48.64) * mm});
            skArc(sketch, "E844.MirrorCS", {"start": v(-155.9, -48.96) * mm, "mid": v(-156.34, -48.31) * mm, "end": v(-156.5, -47.55) * mm});
            skLineSegment(sketch, "E845.MirrorCS", {"start": v(-152.2, -51.04) * mm, "end": v(-153.83, -51.04) * mm});
            skLineSegment(sketch, "E846.MirrorCS", {"start": v(-152.2, -48.64) * mm, "end": v(-150.9, -48.64) * mm});
            skLineSegment(sketch, "E847.MirrorCS", {"start": v(-151.9, -55.54) * mm, "end": v(-154.9, -55.54) * mm});
            skPoint(sketch, "E848.MirrorP", {"position": v(-150.9, -49.14) * mm});
            skLineSegment(sketch, "E849.MirrorCS", {"start": v(-157.3, -53.74) * mm, "end": v(-157.3, -55.04) * mm});
            skLineSegment(sketch, "E850.MirrorCS", {"start": v(-154.9, -53.74) * mm, "end": v(-157.3, -53.74) * mm});
            skLineSegment(sketch, "E851.MirrorCS", {"start": v(-152.2, -51.04) * mm, "end": v(-152.2, -48.64) * mm});
            skLineSegment(sketch, "E852.MirrorCS", {"start": v(-150.4, -54.04) * mm, "end": v(-150.4, -51.04) * mm});
            skLineSegment(sketch, "E853.MirrorCS", {"start": v(-155.9, -48.96) * mm, "end": v(-153.83, -51.04) * mm});
            skPoint(sketch, "E854.MirrorP", {"position": v(-156.5, -48.38) * mm});
            skPoint(sketch, "E855.MirrorP", {"position": v(-150.4, -55.54) * mm});
            skPoint(sketch, "E856.MirrorP", {"position": v(-156.5, -49.44) * mm});
            skLineSegment(sketch, "E857.MirrorCS", {"start": v(-156.97, -50.02) * mm, "end": v(-154.9, -52.1) * mm});
            skPoint(sketch, "E858.MirrorP", {"position": v(-157.56, -49.44) * mm});
            skArc(sketch, "E859.MirrorCS", {"start": v(-150.4, -54.04) * mm, "mid": v(-150.83, -55.1) * mm, "end": v(-151.9, -55.54) * mm});
            skLineSegment(sketch, "E860.MirrorCS", {"start": v(-154.9, -53.74) * mm, "end": v(-154.9, -52.1) * mm});
            skArc(sketch, "E861.MirrorCS", {"start": v(-158.38, -49.44) * mm, "mid": v(-157.62, -49.59) * mm, "end": v(-156.97, -50.02) * mm});
            skLineSegment(sketch, "E862.trimOffspring", {"start": v(-150.4, -41.94) * mm, "end": v(-150.4, -37.04) * mm});
            skLineSegment(sketch, "E863.MirrorCS", {"start": v(-156.8, -35.84) * mm, "end": v(-156.8, -35.54) * mm});
            skArc(sketch, "E864.MirrorCS", {"start": v(-156.8, -35.84) * mm, "mid": v(-156.85, -35.98) * mm, "end": v(-157, -36.04) * mm});
            skLineSegment(sketch, "E865.MirrorCS", {"start": v(-157, -36.04) * mm, "end": v(-157.3, -36.04) * mm});
            skLineSegment(sketch, "E866", {"start": v(-156.3, -35.54) * mm, "end": v(-156.8, -35.54) * mm});
            skLineSegment(sketch, "E867.MirrorCS", {"start": v(-156.8, -55.24) * mm, "end": v(-156.8, -55.54) * mm});
            skLineSegment(sketch, "E868.MirrorCS", {"start": v(-157, -55.04) * mm, "end": v(-157.3, -55.04) * mm});
            skLineSegment(sketch, "E869.MirrorCS", {"start": v(-156.3, -55.54) * mm, "end": v(-156.8, -55.54) * mm});
            skArc(sketch, "E870.MirrorCS", {"start": v(-156.8, -55.24) * mm, "mid": v(-156.85, -55.1) * mm, "end": v(-157, -55.04) * mm});
            skArc(sketch, "E871.MirrorCS", {"start": v(-170.1, -49.14) * mm, "mid": v(-169.95, -49.08) * mm, "end": v(-169.9, -48.94) * mm});
            skLineSegment(sketch, "E872.MirrorCS", {"start": v(-170.1, -41.94) * mm, "end": v(-170.4, -41.94) * mm});
            skLineSegment(sketch, "E873.MirrorCS", {"start": v(-169.9, -48.94) * mm, "end": v(-169.9, -48.64) * mm});
            skArc(sketch, "E874.MirrorCS", {"start": v(-170.1, -41.94) * mm, "mid": v(-169.95, -42) * mm, "end": v(-169.9, -42.14) * mm});
            skLineSegment(sketch, "E875.MirrorCS", {"start": v(-169.9, -42.14) * mm, "end": v(-169.9, -42.44) * mm});
            skLineSegment(sketch, "E876.MirrorCS", {"start": v(-170.1, -49.14) * mm, "end": v(-170.4, -49.14) * mm});
            skLineSegment(sketch, "E877.MirrorCS", {"start": v(-164.5, -35.54) * mm, "end": v(-164, -35.54) * mm});
            skArc(sketch, "E878.MirrorCS", {"start": v(-170.4, -54.04) * mm, "mid": v(-169.96, -55.1) * mm, "end": v(-168.9, -55.54) * mm});
            skLineSegment(sketch, "E879.MirrorCS", {"start": v(-164, -35.84) * mm, "end": v(-164, -35.54) * mm});
            skArc(sketch, "E880.MirrorCS", {"start": v(-164.88, -42.11) * mm, "mid": v(-164.45, -42.76) * mm, "end": v(-164.3, -43.52) * mm});
            skLineSegment(sketch, "E881.MirrorCS", {"start": v(-163.8, -55.04) * mm, "end": v(-163.5, -55.04) * mm});
            skLineSegment(sketch, "E882.MirrorCS", {"start": v(-163.5, -37.34) * mm, "end": v(-163.5, -36.04) * mm});
            skLineSegment(sketch, "E883.MirrorCS", {"start": v(-162.4, -41.64) * mm, "end": v(-158.38, -41.64) * mm});
            skLineSegment(sketch, "E884.MirrorCS", {"start": v(-168.6, -48.64) * mm, "end": v(-169.9, -48.64) * mm});
            skLineSegment(sketch, "E885.MirrorCS", {"start": v(-168.6, -42.44) * mm, "end": v(-169.9, -42.44) * mm});
            skLineSegment(sketch, "E886.MirrorCS", {"start": v(-163.8, -36.04) * mm, "end": v(-163.5, -36.04) * mm});
            skArc(sketch, "E887.MirrorCS", {"start": v(-164.88, -48.96) * mm, "mid": v(-164.45, -48.31) * mm, "end": v(-164.3, -47.55) * mm});
            skArc(sketch, "E888.MirrorCS", {"start": v(-164, -55.24) * mm, "mid": v(-163.94, -55.1) * mm, "end": v(-163.8, -55.04) * mm});
            skArc(sketch, "E889.MirrorCS", {"start": v(-164, -35.84) * mm, "mid": v(-163.94, -35.98) * mm, "end": v(-163.8, -36.04) * mm});
            skLineSegment(sketch, "E890.MirrorCS", {"start": v(-164, -55.24) * mm, "end": v(-164, -55.54) * mm});
            skLineSegment(sketch, "E891.MirrorCS", {"start": v(-162.4, -49.44) * mm, "end": v(-158.38, -49.44) * mm});
            skLineSegment(sketch, "E892.MirrorCS", {"start": v(-164.5, -55.54) * mm, "end": v(-164, -55.54) * mm});
            skLineSegment(sketch, "E893.MirrorCS", {"start": v(-163.5, -53.74) * mm, "end": v(-163.5, -55.04) * mm});
            skArc(sketch, "E894.MirrorCS", {"start": v(-162.4, -41.64) * mm, "mid": v(-163.17, -41.48) * mm, "end": v(-163.82, -41.05) * mm});
            skPoint(sketch, "E895.MirrorP", {"position": v(-170.4, -55.54) * mm});
            skLineSegment(sketch, "E896.MirrorCS", {"start": v(-168.9, -55.54) * mm, "end": v(-164.5, -55.54) * mm});
            skPoint(sketch, "E897.MirrorP", {"position": v(-164.3, -49.44) * mm});
            skLineSegment(sketch, "E898.MirrorCS", {"start": v(-168.9, -35.54) * mm, "end": v(-164.5, -35.54) * mm});
            skArc(sketch, "E899.MirrorCS", {"start": v(-162.4, -49.44) * mm, "mid": v(-163.17, -49.59) * mm, "end": v(-163.82, -50.02) * mm});
            skArc(sketch, "E900.MirrorCS", {"start": v(-170.4, -37.04) * mm, "mid": v(-169.96, -35.98) * mm, "end": v(-168.9, -35.54) * mm});
            skPoint(sketch, "E901.MirrorP", {"position": v(-164.3, -48.38) * mm});
            skLineSegment(sketch, "E902.MirrorCS", {"start": v(-165.9, -37.34) * mm, "end": v(-165.9, -38.98) * mm});
            skLineSegment(sketch, "E903.MirrorCS", {"start": v(-163.82, -41.05) * mm, "end": v(-165.9, -38.98) * mm});
            skPoint(sketch, "E904.MirrorP", {"position": v(-164.3, -42.7) * mm});
            skLineSegment(sketch, "E905.MirrorCS", {"start": v(-168.6, -51.04) * mm, "end": v(-168.6, -48.64) * mm});
            skLineSegment(sketch, "E906.MirrorCS", {"start": v(-164.88, -48.96) * mm, "end": v(-166.96, -51.04) * mm});
            skLineSegment(sketch, "E907.MirrorCS", {"start": v(-165.9, -53.74) * mm, "end": v(-163.5, -53.74) * mm});
            skLineSegment(sketch, "E908.MirrorCS", {"start": v(-168.6, -51.04) * mm, "end": v(-166.96, -51.04) * mm});
            skLineSegment(sketch, "E909.MirrorCS", {"start": v(-170.4, -54.04) * mm, "end": v(-170.4, -51.04) * mm});
            skLineSegment(sketch, "E910.MirrorCS", {"start": v(-168.9, -35.54) * mm, "end": v(-165.9, -35.54) * mm});
            skLineSegment(sketch, "E911.MirrorCS", {"start": v(-170.4, -41.94) * mm, "end": v(-170.4, -37.04) * mm});
            skLineSegment(sketch, "E912.MirrorCS", {"start": v(-165.9, -37.34) * mm, "end": v(-163.5, -37.34) * mm});
            skLineSegment(sketch, "E913.MirrorCS", {"start": v(-163.82, -50.02) * mm, "end": v(-165.9, -52.1) * mm});
            skPoint(sketch, "E914.MirrorP", {"position": v(-163.23, -49.44) * mm});
            skLineSegment(sketch, "E915.MirrorCS", {"start": v(-168.6, -40.04) * mm, "end": v(-168.6, -42.44) * mm});
            skLineSegment(sketch, "E916.MirrorCS", {"start": v(-170.4, -37.04) * mm, "end": v(-170.4, -40.04) * mm});
            skPoint(sketch, "E917.MirrorP", {"position": v(-169.9, -49.14) * mm});
            skPoint(sketch, "E918.MirrorP", {"position": v(-170.4, -35.54) * mm});
            skPoint(sketch, "E919.MirrorP", {"position": v(-169.9, -41.94) * mm});
            skLineSegment(sketch, "E920.MirrorCS", {"start": v(-164.88, -42.11) * mm, "end": v(-166.96, -40.04) * mm});
            skLineSegment(sketch, "E921.MirrorCS", {"start": v(-168.6, -40.04) * mm, "end": v(-166.96, -40.04) * mm});
            skLineSegment(sketch, "E922.MirrorCS", {"start": v(-170.4, -54.04) * mm, "end": v(-170.4, -49.14) * mm});
            skLineSegment(sketch, "E923.MirrorCS", {"start": v(-168.9, -55.54) * mm, "end": v(-165.9, -55.54) * mm});
            skPoint(sketch, "E924.MirrorP", {"position": v(-164.3, -41.64) * mm});
            skPoint(sketch, "E925.MirrorP", {"position": v(-163.23, -41.64) * mm});
            skLineSegment(sketch, "E926.MirrorCS", {"start": v(-165.9, -53.74) * mm, "end": v(-165.9, -52.1) * mm});
            skSolve(sketch);
        }
        {
            var Q0;
            Q0=makeQuery(id+"F16.imprint","IMPRINT",FACE,{"disambiguationData":[TD([[makeQuery(id+"F16.imprint","IMPRINT",EDGE,{"derivedFrom":sQuery(id+"F16.wireOp",EDGE,"E825.bottom")}),-1.0]])]});
            extrude(context, id + "F17", {"entities" : qUnion([Q0]), "endBound" : BoundingType.SYMMETRIC, "depth" : 212 * mm, "offsetDistance" : 25 * mm});
        }
        {
            var Q0;
            Q0=qCreatedBy(makeId("Top.planeOp"),FACE);
            var sketch = newSketch(context, id + "F18", { "sketchPlane" : qUnion([Q0])});
            skCircle(sketch, "E927", {"center": v(10.47, 96.92) * mm, "radius": 2.5 * mm});
            skLineSegment(sketch, "E928.bottom", {"start": v(18.97, 86.92) * mm, "end": v(14.57, 86.92) * mm});
            skLineSegment(sketch, "E928.top", {"start": v(18.97, 106.92) * mm, "end": v(14.57, 106.92) * mm});
            skLineSegment(sketch, "E928.left", {"start": v(20.47, 88.42) * mm, "end": v(20.47, 93.32) * mm});
            skLineSegment(sketch, "E929.bottom", {"start": v(12.48, 93.02) * mm, "end": v(8.46, 93.02) * mm});
            skLineSegment(sketch, "E929.top", {"start": v(12.48, 100.82) * mm, "end": v(8.46, 100.82) * mm});
            skLineSegment(sketch, "E929.left", {"start": v(14.37, 94.9) * mm, "end": v(14.37, 98.93) * mm});
            skLineSegment(sketch, "E929.right", {"start": v(6.57, 94.9) * mm, "end": v(6.57, 98.93) * mm});
            skLineSegment(sketch, "E930.bottom", {"start": v(18.97, 106.92) * mm, "end": v(15.97, 106.92) * mm});
            skLineSegment(sketch, "E930.left", {"start": v(20.47, 105.42) * mm, "end": v(20.47, 102.42) * mm});
            skLineSegment(sketch, "E930.right", {"start": v(15.97, 105.12) * mm, "end": v(15.97, 103.48) * mm});
            skLineSegment(sketch, "E931", {"start": v(14.96, 100.35) * mm, "end": v(17.03, 102.42) * mm});
            skLineSegment(sketch, "E932.MirrorCS", {"start": v(13.9, 101.4) * mm, "end": v(15.97, 103.48) * mm});
            skLineSegment(sketch, "E933", {"start": v(18.67, 102.42) * mm, "end": v(18.67, 100.02) * mm});
            skLineSegment(sketch, "E934", {"start": v(20.17, 100.52) * mm, "end": v(20.47, 100.52) * mm});
            skLineSegment(sketch, "E935", {"start": v(18.67, 100.02) * mm, "end": v(19.97, 100.02) * mm});
            skLineSegment(sketch, "E936", {"start": v(19.97, 100.32) * mm, "end": v(19.97, 100.02) * mm});
            skPoint(sketch, "E937.visualSharp", {"position": v(19.97, 100.52) * mm});
            skArc(sketch, "E937.filletArc", {"start": v(20.17, 100.52) * mm, "mid": v(20.03, 100.46) * mm, "end": v(19.97, 100.32) * mm});
            skPoint(sketch, "E938.newPointA", {"position": v(14.37, 99.76) * mm});
            skArc(sketch, "E938.filletArc", {"start": v(14.96, 100.35) * mm, "mid": v(14.53, 99.7) * mm, "end": v(14.37, 98.93) * mm});
            skPoint(sketch, "E939.newPointA", {"position": v(13.31, 100.82) * mm});
            skPoint(sketch, "E939.newPointB", {"position": v(14.37, 100.82) * mm});
            skArc(sketch, "E939.filletArc", {"start": v(12.48, 100.82) * mm, "mid": v(13.25, 100.97) * mm, "end": v(13.9, 101.4) * mm});
            skLineSegment(sketch, "E940.MirrorCS", {"start": v(15.97, 105.12) * mm, "end": v(13.57, 105.12) * mm});
            skLineSegment(sketch, "E941.MirrorCS", {"start": v(13.57, 105.12) * mm, "end": v(13.57, 106.42) * mm});
            skPoint(sketch, "E942.visualSharp", {"position": v(20.47, 106.92) * mm});
            skArc(sketch, "E942.filletArc", {"start": v(20.47, 105.42) * mm, "mid": v(20.03, 106.48) * mm, "end": v(18.97, 106.92) * mm});
            skLineSegment(sketch, "E943.trimOffspring", {"start": v(18.67, 102.42) * mm, "end": v(17.03, 102.42) * mm});
            skLineSegment(sketch, "E944.MirrorCS", {"start": v(20.17, 93.32) * mm, "end": v(20.47, 93.32) * mm});
            skArc(sketch, "E945.MirrorCS", {"start": v(20.17, 93.32) * mm, "mid": v(20.03, 93.38) * mm, "end": v(19.97, 93.52) * mm});
            skLineSegment(sketch, "E946.MirrorCS", {"start": v(19.97, 93.52) * mm, "end": v(19.97, 93.82) * mm});
            skArc(sketch, "E947.MirrorCS", {"start": v(14.96, 93.5) * mm, "mid": v(14.53, 94.14) * mm, "end": v(14.37, 94.9) * mm});
            skLineSegment(sketch, "E948.MirrorCS", {"start": v(18.67, 91.42) * mm, "end": v(17.03, 91.42) * mm});
            skLineSegment(sketch, "E949.MirrorCS", {"start": v(18.67, 93.82) * mm, "end": v(19.97, 93.82) * mm});
            skLineSegment(sketch, "E950.MirrorCS", {"start": v(18.97, 86.92) * mm, "end": v(15.97, 86.92) * mm});
            skPoint(sketch, "E951.MirrorP", {"position": v(19.97, 93.32) * mm});
            skLineSegment(sketch, "E952.MirrorCS", {"start": v(13.57, 88.72) * mm, "end": v(13.57, 87.42) * mm});
            skLineSegment(sketch, "E953.MirrorCS", {"start": v(15.97, 88.72) * mm, "end": v(13.57, 88.72) * mm});
            skLineSegment(sketch, "E954.MirrorCS", {"start": v(18.67, 91.42) * mm, "end": v(18.67, 93.82) * mm});
            skLineSegment(sketch, "E955.MirrorCS", {"start": v(20.47, 88.42) * mm, "end": v(20.47, 91.42) * mm});
            skLineSegment(sketch, "E956.MirrorCS", {"start": v(14.96, 93.5) * mm, "end": v(17.03, 91.42) * mm});
            skPoint(sketch, "E957.MirrorP", {"position": v(14.37, 94.08) * mm});
            skPoint(sketch, "E958.MirrorP", {"position": v(20.47, 86.92) * mm});
            skPoint(sketch, "E959.MirrorP", {"position": v(14.37, 93.02) * mm});
            skLineSegment(sketch, "E960.MirrorCS", {"start": v(13.9, 92.43) * mm, "end": v(15.97, 90.36) * mm});
            skPoint(sketch, "E961.MirrorP", {"position": v(13.31, 93.02) * mm});
            skArc(sketch, "E962.MirrorCS", {"start": v(20.47, 88.42) * mm, "mid": v(20.03, 87.36) * mm, "end": v(18.97, 86.92) * mm});
            skLineSegment(sketch, "E963.MirrorCS", {"start": v(15.97, 88.72) * mm, "end": v(15.97, 90.36) * mm});
            skArc(sketch, "E964.MirrorCS", {"start": v(12.48, 93.02) * mm, "mid": v(13.25, 92.87) * mm, "end": v(13.9, 92.43) * mm});
            skLineSegment(sketch, "E965.trimOffspring", {"start": v(20.47, 100.52) * mm, "end": v(20.47, 105.42) * mm});
            skLineSegment(sketch, "E966.MirrorCS", {"start": v(14.07, 106.62) * mm, "end": v(14.07, 106.92) * mm});
            skArc(sketch, "E967.MirrorCS", {"start": v(14.07, 106.62) * mm, "mid": v(14.02, 106.48) * mm, "end": v(13.87, 106.42) * mm});
            skLineSegment(sketch, "E968.MirrorCS", {"start": v(13.87, 106.42) * mm, "end": v(13.57, 106.42) * mm});
            skLineSegment(sketch, "E969", {"start": v(14.57, 106.92) * mm, "end": v(14.07, 106.92) * mm});
            skLineSegment(sketch, "E970.MirrorCS", {"start": v(14.07, 87.22) * mm, "end": v(14.07, 86.92) * mm});
            skLineSegment(sketch, "E971.MirrorCS", {"start": v(13.87, 87.42) * mm, "end": v(13.57, 87.42) * mm});
            skLineSegment(sketch, "E972.MirrorCS", {"start": v(14.57, 86.92) * mm, "end": v(14.07, 86.92) * mm});
            skArc(sketch, "E973.MirrorCS", {"start": v(14.07, 87.22) * mm, "mid": v(14.02, 87.36) * mm, "end": v(13.87, 87.42) * mm});
            skArc(sketch, "E974.MirrorCS", {"start": v(0.77, 93.32) * mm, "mid": v(0.92, 93.38) * mm, "end": v(0.97, 93.52) * mm});
            skLineSegment(sketch, "E975.MirrorCS", {"start": v(0.77, 100.52) * mm, "end": v(0.47, 100.52) * mm});
            skLineSegment(sketch, "E976.MirrorCS", {"start": v(0.97, 93.52) * mm, "end": v(0.97, 93.82) * mm});
            skArc(sketch, "E977.MirrorCS", {"start": v(0.77, 100.52) * mm, "mid": v(0.92, 100.46) * mm, "end": v(0.97, 100.32) * mm});
            skLineSegment(sketch, "E978.MirrorCS", {"start": v(0.97, 100.32) * mm, "end": v(0.97, 100.02) * mm});
            skLineSegment(sketch, "E979.MirrorCS", {"start": v(0.77, 93.32) * mm, "end": v(0.47, 93.32) * mm});
            skLineSegment(sketch, "E980.MirrorCS", {"start": v(6.37, 106.92) * mm, "end": v(6.87, 106.92) * mm});
            skArc(sketch, "E981.MirrorCS", {"start": v(0.47, 88.42) * mm, "mid": v(0.91, 87.36) * mm, "end": v(1.97, 86.92) * mm});
            skLineSegment(sketch, "E982.MirrorCS", {"start": v(6.87, 106.62) * mm, "end": v(6.87, 106.92) * mm});
            skArc(sketch, "E983.MirrorCS", {"start": v(5.99, 100.35) * mm, "mid": v(6.42, 99.7) * mm, "end": v(6.57, 98.93) * mm});
            skLineSegment(sketch, "E984.MirrorCS", {"start": v(7.07, 87.42) * mm, "end": v(7.37, 87.42) * mm});
            skLineSegment(sketch, "E985.MirrorCS", {"start": v(7.37, 105.12) * mm, "end": v(7.37, 106.42) * mm});
            skLineSegment(sketch, "E986.MirrorCS", {"start": v(8.46, 100.82) * mm, "end": v(12.48, 100.82) * mm});
            skLineSegment(sketch, "E987.MirrorCS", {"start": v(2.27, 93.82) * mm, "end": v(0.97, 93.82) * mm});
            skLineSegment(sketch, "E988.MirrorCS", {"start": v(2.27, 100.02) * mm, "end": v(0.97, 100.02) * mm});
            skLineSegment(sketch, "E989.MirrorCS", {"start": v(7.07, 106.42) * mm, "end": v(7.37, 106.42) * mm});
            skArc(sketch, "E990.MirrorCS", {"start": v(5.99, 93.5) * mm, "mid": v(6.42, 94.14) * mm, "end": v(6.57, 94.9) * mm});
            skArc(sketch, "E991.MirrorCS", {"start": v(6.87, 87.22) * mm, "mid": v(6.93, 87.36) * mm, "end": v(7.07, 87.42) * mm});
            skArc(sketch, "E992.MirrorCS", {"start": v(6.87, 106.62) * mm, "mid": v(6.93, 106.48) * mm, "end": v(7.07, 106.42) * mm});
            skLineSegment(sketch, "E993.MirrorCS", {"start": v(6.87, 87.22) * mm, "end": v(6.87, 86.92) * mm});
            skLineSegment(sketch, "E994.MirrorCS", {"start": v(8.46, 93.02) * mm, "end": v(12.48, 93.02) * mm});
            skLineSegment(sketch, "E995.MirrorCS", {"start": v(6.37, 86.92) * mm, "end": v(6.87, 86.92) * mm});
            skLineSegment(sketch, "E996.MirrorCS", {"start": v(7.37, 88.72) * mm, "end": v(7.37, 87.42) * mm});
            skArc(sketch, "E997.MirrorCS", {"start": v(8.46, 100.82) * mm, "mid": v(7.7, 100.97) * mm, "end": v(7.05, 101.4) * mm});
            skPoint(sketch, "E998.MirrorP", {"position": v(0.47, 86.92) * mm});
            skLineSegment(sketch, "E999.MirrorCS", {"start": v(1.97, 86.92) * mm, "end": v(6.37, 86.92) * mm});
            skPoint(sketch, "E1000.MirrorP", {"position": v(6.57, 93.02) * mm});
            skLineSegment(sketch, "E1001.MirrorCS", {"start": v(1.97, 106.92) * mm, "end": v(6.37, 106.92) * mm});
            skArc(sketch, "E1002.MirrorCS", {"start": v(8.46, 93.02) * mm, "mid": v(7.7, 92.87) * mm, "end": v(7.05, 92.43) * mm});
            skArc(sketch, "E1003.MirrorCS", {"start": v(0.47, 105.42) * mm, "mid": v(0.91, 106.48) * mm, "end": v(1.97, 106.92) * mm});
            skPoint(sketch, "E1004.MirrorP", {"position": v(6.57, 94.08) * mm});
            skLineSegment(sketch, "E1005.MirrorCS", {"start": v(4.97, 105.12) * mm, "end": v(4.97, 103.48) * mm});
            skLineSegment(sketch, "E1006.MirrorCS", {"start": v(7.05, 101.4) * mm, "end": v(4.97, 103.48) * mm});
            skPoint(sketch, "E1007.MirrorP", {"position": v(6.57, 99.76) * mm});
            skLineSegment(sketch, "E1008.MirrorCS", {"start": v(2.27, 91.42) * mm, "end": v(2.27, 93.82) * mm});
            skLineSegment(sketch, "E1009.MirrorCS", {"start": v(5.99, 93.5) * mm, "end": v(3.91, 91.42) * mm});
            skLineSegment(sketch, "E1010.MirrorCS", {"start": v(4.97, 88.72) * mm, "end": v(7.37, 88.72) * mm});
            skLineSegment(sketch, "E1011.MirrorCS", {"start": v(2.27, 91.42) * mm, "end": v(3.91, 91.42) * mm});
            skLineSegment(sketch, "E1012.MirrorCS", {"start": v(0.47, 88.42) * mm, "end": v(0.47, 91.42) * mm});
            skLineSegment(sketch, "E1013.MirrorCS", {"start": v(1.97, 106.92) * mm, "end": v(4.97, 106.92) * mm});
            skLineSegment(sketch, "E1014.MirrorCS", {"start": v(0.47, 100.52) * mm, "end": v(0.47, 105.42) * mm});
            skLineSegment(sketch, "E1015.MirrorCS", {"start": v(4.97, 105.12) * mm, "end": v(7.37, 105.12) * mm});
            skLineSegment(sketch, "E1016.MirrorCS", {"start": v(7.05, 92.43) * mm, "end": v(4.97, 90.36) * mm});
            skPoint(sketch, "E1017.MirrorP", {"position": v(7.63, 93.02) * mm});
            skLineSegment(sketch, "E1018.MirrorCS", {"start": v(2.27, 102.42) * mm, "end": v(2.27, 100.02) * mm});
            skLineSegment(sketch, "E1019.MirrorCS", {"start": v(0.47, 105.42) * mm, "end": v(0.47, 102.42) * mm});
            skPoint(sketch, "E1020.MirrorP", {"position": v(0.97, 93.32) * mm});
            skPoint(sketch, "E1021.MirrorP", {"position": v(0.47, 106.92) * mm});
            skPoint(sketch, "E1022.MirrorP", {"position": v(0.97, 100.52) * mm});
            skLineSegment(sketch, "E1023.MirrorCS", {"start": v(5.99, 100.35) * mm, "end": v(3.91, 102.42) * mm});
            skLineSegment(sketch, "E1024.MirrorCS", {"start": v(2.27, 102.42) * mm, "end": v(3.91, 102.42) * mm});
            skLineSegment(sketch, "E1025.MirrorCS", {"start": v(0.47, 88.42) * mm, "end": v(0.47, 93.32) * mm});
            skLineSegment(sketch, "E1026.MirrorCS", {"start": v(1.97, 86.92) * mm, "end": v(4.97, 86.92) * mm});
            skPoint(sketch, "E1027.MirrorP", {"position": v(6.57, 100.82) * mm});
            skPoint(sketch, "E1028.MirrorP", {"position": v(7.63, 100.82) * mm});
            skLineSegment(sketch, "E1029.MirrorCS", {"start": v(4.97, 88.72) * mm, "end": v(4.97, 90.36) * mm});
            skSolve(sketch);
        }
        {
            var Q0;
            Q0=makeQuery(id+"F18.imprint","IMPRINT",FACE,{"disambiguationData":[TD([[makeQuery(id+"F18.imprint","IMPRINT",EDGE,{"derivedFrom":sQuery(id+"F18.wireOp",EDGE,"E928.bottom")}),-1.0]])]});
            extrude(context, id + "F19", {"entities" : qUnion([Q0]), "endBound" : BoundingType.SYMMETRIC, "depth" : 199 * mm, "offsetDistance" : 25 * mm});
        }
    });
